FCSTD DOCUMENT  (FreeCAD 1.0R39319 (Git))
Label: Assy_PiTrac
License: All rights reserved
LicenseURL: https://en.wikipedia.org/wiki/All_rights_reserved
objects: TechDraw::DrawViewBalloon×30, App::Link×9, TechDraw::DrawProjGroupItem×6, TechDraw::DrawViewDimension×6, App::DocumentObjectGroup×3, TechDraw::DrawSVGTemplate×2, TechDraw::DrawViewSection×2, TechDraw::DrawViewAnnotation×2, TechDraw::DrawPage×2, PartDesign::CoordinateSystem×1, App::FeaturePython×1, App::Part×1, Spreadsheet::Sheet×1, TechDraw::DrawProjGroup×1, TechDraw::DrawViewSpreadsheet×1, TechDraw::DrawViewDimExtent×1
note: 15 computed .brp shape members not serialized (recipe doc carries the construction recipe); baked Part::Feature solids carry a one-line shape summary decoded from their .brp
EXTERNAL_REF file=Assy_Stack_Module_PSU.FCStd obj=LCS_Origin
EXTERNAL_REF file=Assy_Stack_Module_PSU.FCStd obj=Assembly
EXTERNAL_REF file=Assy_Stack_Module_Flight_Cam.FCStd obj=LCS_Origin
EXTERNAL_REF file=Assy_Stack_Module_Flight_Cam.FCStd obj=Assembly
EXTERNAL_REF file=Assy_Stack_Module_LED.FCStd obj=LCS_Origin
EXTERNAL_REF file=Assy_Stack_Module_LED.FCStd obj=Assembly
EXTERNAL_REF file=Assy_Stack_Module_Tee_Cam.FCStd obj=LCS_Origin
EXTERNAL_REF file=Assy_Stack_Module_Tee_Cam.FCStd obj=Assembly
EXTERNAL_REF file=Assy_Stack_Module_Cover_forInserts.FCStd obj=LCS_Origin
EXTERNAL_REF file=Assy_Stack_Module_Cover_forInserts.FCStd obj=Assembly
EXTERNAL_REF file=Assy_RaspberryPi5_carrier.FCStd obj=LCS_Origin
EXTERNAL_REF file=Assy_RaspberryPi5_carrier.FCStd obj=Assembly
EXTERNAL_REF file=Assy_V3Connector_Board.FCStd obj=LCS_Origin
EXTERNAL_REF file=Assy_V3Connector_Board.FCStd obj=Assembly
EXTERNAL_REF file=../../Part/Purchase/Acrylic_Backplate.FCStd obj=LCS_1
EXTERNAL_REF file=../../Part/Purchase/Acrylic_Backplate.FCStd obj=Part
EXTERNAL_REF file=../../Part/Purchase/Shank_Shield.FCStd obj=LCS_1
EXTERNAL_REF file=../../Part/Purchase/Shank_Shield.FCStd obj=Part

FEATURE [App::DocumentObjectGroup] Parts
FEATURE [PartDesign::CoordinateSystem] LCS_Origin
  AttacherType = Attacher::AttachEngine3D
  AttachmentSupport = -> [X_Axis]
  MapMode = 2
FEATURE [App::DocumentObjectGroup] Constraints
FEATURE [App::FeaturePython] Variables  # WARN: FeaturePython — macro-defined, semantics opaque (R4)
  Type = App::PropertyContainer
FEATURE [App::DocumentObjectGroup] Configurations
FEATURE [App::Link] Assy_Stack_Module_PSU
  AttachedBy = #LCS_Origin
  AttachedTo = Parent Assembly#LCS_Origin
  LinkedObject = -> <external Assy_Stack_Module_PSU.FCStd>#Assembly
  SolverId = Asm4EE
  expr: Placement = LCS_Origin.Placement * AttachmentOffset * Assy_Stack_Module_PSU#LCS_Origin.Placement ^ -1
FEATURE [App::Link] Assy_Stack_Module_Flight_Cam
  AttachedBy = #LCS_Origin
  AttachedTo = Assy_Stack_Module_PSU#LCS_Origin
  AttachmentOffset = pos=(116.5,43.25,33.5) rot=(-0.57735,0.57735,-0.57735;4.18879rad)
  LinkPlacement = pos=(116.5,43.25,33.5) rot=(-0.57735,0.57735,-0.57735;4.18879rad)
  LinkedObject = -> <external Assy_Stack_Module_Flight_Cam.FCStd>#Assembly
  Placement = pos=(116.5,43.25,33.5) rot=(-0.57735,0.57735,-0.57735;4.18879rad)
  SolverId = Asm4EE
  expr: Placement = Assy_Stack_Module_PSU.Placement * Assy_Stack_Module_PSU#LCS_Origin.Placement * AttachmentOffset * Assy_Stack_Module_Flight_Cam#LCS_Origin.Placement ^ -1
FEATURE [App::Link] Assy_Stack_Module_LED
  AttachedBy = #LCS_Origin
  AttachedTo = Assy_Stack_Module_Flight_Cam#LCS_Origin
  AttachmentOffset = pos=(0,0,-87.5) rot=(0,0,1;0rad)
  LinkPlacement = pos=(116.5,130.75,33.5) rot=(-0.57735,0.57735,-0.57735;4.18879rad)
  LinkedObject = -> <external Assy_Stack_Module_LED.FCStd>#Assembly
  Placement = pos=(116.5,130.75,33.5) rot=(-0.57735,0.57735,-0.57735;4.18879rad)
  SolverId = Asm4EE
  expr: Placement = Assy_Stack_Module_Flight_Cam.Placement * Assy_Stack_Module_Flight_Cam#LCS_Origin.Placement * AttachmentOffset * Assy_Stack_Module_LED#LCS_Origin.Placement ^ -1
FEATURE [App::Link] Assy_Stack_Module_Tee_Cam
  AttachedBy = #LCS_Origin
  AttachedTo = Assy_Stack_Module_LED#LCS_Origin
  AttachmentOffset = pos=(0,0,-87.5) rot=(0,0,1;0rad)
  LinkPlacement = pos=(116.5,218.25,33.5) rot=(-0.57735,0.57735,-0.57735;4.18879rad)
  LinkedObject = -> <external Assy_Stack_Module_Tee_Cam.FCStd>#Assembly
  Placement = pos=(116.5,218.25,33.5) rot=(-0.57735,0.57735,-0.57735;4.18879rad)
  SolverId = Asm4EE
  expr: Placement = Assy_Stack_Module_LED.Placement * Assy_Stack_Module_LED#LCS_Origin.Placement * AttachmentOffset * Assy_Stack_Module_Tee_Cam#LCS_Origin.Placement ^ -1
FEATURE [App::Link] Assy_Stack_Module_Cover_forInserts
  AttachedBy = #LCS_Origin
  AttachedTo = Assy_Stack_Module_Tee_Cam#LCS_Origin
  AttachmentOffset = pos=(82.5,-13.5,-84.5) rot=(0.57735,-0.57735,0.57735;2.0944rad)
  LinkPlacement = pos=(130,302.75,116) rot=(-0.57735,0.57735,-0.57735;2.0944rad)
  LinkedObject = -> <external Assy_Stack_Module_Cover_forInserts.FCStd>#Assembly
  Placement = pos=(130,302.75,116) rot=(-0.57735,0.57735,-0.57735;2.0944rad)
  SolverId = Asm4EE
  expr: Placement = Assy_Stack_Module_Tee_Cam.Placement * Assy_Stack_Module_Tee_Cam#LCS_Origin.Placement * AttachmentOffset * Assy_Stack_Module_Cover_forInserts#LCS_Origin.Placement ^ -1
FEATURE [App::Link] Assy_RaspberryPi5_carrier
  AttachedBy = #LCS_Origin
  AttachedTo = Assy_Stack_Module_Tee_Cam#LCS_Origin
  AttachmentOffset = pos=(45,105,-38.5) rot=(0.57735,-0.57735,0.57735;4.18879rad)
  LinkPlacement = pos=(11.5,256.75,78.5) rot=(0,0,1;0rad)
  LinkedObject = -> <external Assy_RaspberryPi5_carrier.FCStd>#Assembly
  Placement = pos=(11.5,256.75,78.5) rot=(0,0,1;0rad)
  SolverId = Asm4EE
  expr: Placement = Assy_Stack_Module_Tee_Cam.Placement * Assy_Stack_Module_Tee_Cam#LCS_Origin.Placement * AttachmentOffset * Assy_RaspberryPi5_carrier#LCS_Origin.Placement ^ -1
FEATURE [App::Link] Assy_V3Connector_Board
  AttachedBy = #LCS_Origin
  AttachedTo = Assy_Stack_Module_Flight_Cam#LCS_Origin
  AttachmentOffset = pos=(52,50,-55) rot=(0.707107,-0.707107,0;3.14159rad)
  LinkPlacement = pos=(66.5,98.25,85.5) rot=(-1,0,0;1.5708rad)
  LinkedObject = -> <external Assy_V3Connector_Board.FCStd>#Assembly
  Placement = pos=(66.5,98.25,85.5) rot=(-1,0,0;1.5708rad)
  SolverId = Asm4EE
  expr: Placement = Assy_Stack_Module_Flight_Cam.Placement * Assy_Stack_Module_Flight_Cam#LCS_Origin.Placement * AttachmentOffset * Assy_V3Connector_Board#LCS_Origin.Placement ^ -1
FEATURE [App::Link] Acrylic_Backplate
  AttachedBy = #LCS_1
  AttachedTo = Parent Assembly#LCS_Origin
  AttachmentOffset = pos=(11,37,117) rot=(0,0,1;0rad)
  LinkPlacement = pos=(11,37,117) rot=(0,0,1;0rad)
  LinkedObject = -> <external ../../Part/Purchase/Acrylic_Backplate.FCStd>#Part
  Placement = pos=(11,37,117) rot=(0,0,1;0rad)
  SolverId = Asm4EE
  expr: Placement = LCS_Origin.Placement * AttachmentOffset * Acrylic_Backplate#LCS_1.Placement ^ -1
FEATURE [App::Link] Shank_Shield
  AttachedBy = #LCS_1
  AttachedTo = Parent Assembly#LCS_Origin
  AttachmentOffset = pos=(-3,40,-13) rot=(0,0,1;0rad)
  LinkPlacement = pos=(-3,40,-13) rot=(0,0,1;0rad)
  LinkedObject = -> <external ../../Part/Purchase/Shank_Shield.FCStd>#Part
  Placement = pos=(-3,40,-13) rot=(0,0,1;0rad)
  SolverId = Asm4EE
  expr: Placement = LCS_Origin.Placement * AttachmentOffset * Shank_Shield#LCS_1.Placement ^ -1
FEATURE [App::Part] Assembly  label="Assy_PiTrac"
  AssemblyType = Part::Link
  Group = -> [LCS_Origin,Constraints,Variables,Configurations,Assy_Stack_Module_PSU,Assy_Stack_Module_Flight_Cam,Assy_Stack_Module_LED,Assy_Stack_Module_Tee_Cam,Assy_Stack_Module_Cover_forInserts,Assy_RaspberryPi5_carrier,Assy_V3Connector_Board,Acrylic_Backplate,Shank_Shield]
  Origin = -> Origin
  Type = Assembly
FEATURE [Spreadsheet::Sheet] Spreadsheet  label="BOM"
  cells = A1=16; B1=1; C1='Acrylic Backplate; A2=15; B2=1; C2='Acrylic Shankshield; A3=14; B3=4; C3='M5x306 mm rod; D3==306 mm; A4=13; B4=4; C4='M5 x 12 mm sleeve nut; A5=12; B5=4; C5='ISO 7380-2 M5x10 mm screw; D5='10 mm; ISO 4762 optional; A6=11; B6=12; C6='ISO 7380-2 M5x15 mm screw; D6='10–15 mm; ISO 4762 optional; A7=10; B7=4; C7='ISO 10511 M5 lock nut; A8=9; B8=4; C8='ISO 4032 M5 nut; A9=8; B9=4; C9='Foot; E9='PETG or PLA; A10=7; B10=4; C10='Carrier_Clamps; E10='PETG or PLA; A11=6; B11=1; C11='Pi 5 Assembly; A12=5; B12=1; C12='ConnectorBoardv3 Assembly; A13=4; B13=1; C13='Stack Module Cover Assembly; A14=3; B14=1; C14='PSU Stack Module Assembly; D14='-; A15=2; B15=1; C15='LED Stack Module Assembly; D15='-; A16=1; B16=2; C16='Camera Stack Module Assembly; D16='-; A17='Position; B17='Quantity; C17='Part; D17='Dimensions; E17='Material
FEATURE [TechDraw::DrawSVGTemplate] Template
  EditableTexts = approval_person=GitHub PR; creator=Stefan; date_of_issue=20.03.2026; document_type=Assembly Drawing; general_tolerances=na; identification_number=na; language_code=EN; part_material=na; revision_index=AAA; scale=1 : 1; sheet_number=1 / 1; title=Assy_PiTrac
  Height = 594
  Orientation = 1
  Template = <userpath>/Documents/PiTrac/3D Printed Parts/Enclosure Version 3/Assets/PiTrac_A1_Landscape_ISO5457_minimal.svg
  Width = 841
FEATURE [TechDraw::DrawProjGroupItem] View
  CoarseView = false
  Direction = (-0.57735,0.57735,-0.57735)
  Focus = 100
  HardHidden = false
  IsoCount = 0
  IsoHidden = false
  IsoVisible = false
  LockPosition = false
  Perspective = false
  Rotation = 0
  RotationVector = (1,0,0)
  Scale = 0.5
  ScaleType = 2
  ScrubCount = 1
  SeamHidden = false
  SeamVisible = false
  SmoothHidden = false
  SmoothVisible = true
  Source = -> [Assembly]
  Type = 0
  X = 552.509
  XDirection = (-0.707106,0,0.707106)
  Y = 140.759
FEATURE [TechDraw::DrawProjGroupItem] View001  label="Front"
  CoarseView = false
  Direction = (0,0,-1)
  Focus = 100
  HardHidden = false
  IsoCount = 0
  IsoHidden = false
  IsoVisible = false
  LockPosition = true
  Perspective = false
  Rotation = 0
  RotationVector = (1,0,0)
  Scale = 0.5
  ScaleType = 2
  ScrubCount = 1
  SeamHidden = false
  SeamVisible = false
  SmoothHidden = false
  SmoothVisible = true
  Source = -> [Assembly]
  Type = 0
  X = 0
  XDirection = (-1,0,0)
  Y = 0
FEATURE [TechDraw::DrawProjGroupItem] ProjItem  label="Left"
  CoarseView = false
  Direction = (1,0,-1e-16)
  Focus = 100
  HardHidden = false
  IsoCount = 0
  IsoHidden = false
  IsoVisible = false
  LockPosition = false
  Perspective = false
  Rotation = 0
  RotationVector = (1,0,0)
  Scale = 0.5
  ScaleType = 2
  ScrubCount = 1
  SeamHidden = false
  SeamVisible = false
  SmoothHidden = false
  SmoothVisible = true
  Source = -> [Assembly]
  Type = 1
  X = 101
  XDirection = (-1e-16,0,-1)
  Y = 0
FEATURE [TechDraw::DrawProjGroupItem] ProjItem001  label="Rear"
  CoarseView = false
  Direction = (0,0,1)
  Focus = 100
  HardHidden = false
  IsoCount = 0
  IsoHidden = false
  IsoVisible = false
  LockPosition = false
  Perspective = false
  Rotation = 0
  RotationVector = (1,0,0)
  Scale = 0.5
  ScaleType = 2
  ScrubCount = 1
  SeamHidden = false
  SeamVisible = false
  SmoothHidden = false
  SmoothVisible = true
  Source = -> [Assembly]
  Type = 3
  X = 202
  XDirection = (1,0,0)
  Y = 0
FEATURE [TechDraw::DrawProjGroupItem] ProjItem002  label="Top"
  CoarseView = false
  Direction = (0,1,0)
  Focus = 100
  HardHidden = false
  IsoCount = 0
  IsoHidden = false
  IsoVisible = false
  LockPosition = false
  Perspective = false
  Rotation = 0
  RotationVector = (1,0,0)
  Scale = 0.5
  ScaleType = 2
  ScrubCount = 1
  SeamHidden = false
  SeamVisible = false
  SmoothHidden = false
  SmoothVisible = true
  Source = -> [Assembly]
  Type = 4
  X = 0
  XDirection = (-1,0,0)
  Y = -146.779
FEATURE [TechDraw::DrawProjGroup] ProjGroup
  Anchor = -> View001
  AutoDistribute = true
  LockPosition = false
  ProjectionType = 0
  Rotation = 0
  Scale = 0.5
  ScaleType = 2
  Source = -> [Assembly]
  Views = -> [View001,ProjItem,ProjItem001,ProjItem002]
  X = 169.846
  Y = 386.4
  spacingX = 15
  spacingY = 15
FEATURE [TechDraw::DrawViewSection] SectionView  label="Section A - A"
  BaseView = -> View001
  CoarseView = false
  CutSurfaceDisplay = 2
  Direction = (1,-1e-16,0)
  FileGeomPattern = <path>\data\Mod/TechDraw/PAT/FCPAT.pat
  FileHatchPattern = <path>\data\Mod/TechDraw/Patterns/simple.svg
  Focus = 100
  FuseBeforeCut = false
  HardHidden = false
  HatchOffset = (0,0,0)
  HatchRotation = 0
  HatchScale = 1
  IsoCount = 0
  IsoHidden = false
  IsoVisible = false
  LockPosition = false
  NameGeomPattern = Diamond
  Perspective = false
  Rotation = -90
  Scale = 0.5
  ScaleType = 2
  ScrubCount = 1
  SeamHidden = false
  SeamVisible = false
  SectionDirection = 4
  SectionLineStretch = 1
  SectionNormal = (1,-1e-16,0)
  SectionOrigin = (66.5,164.89,48.5)
  SectionSymbol = A
  SmoothHidden = false
  SmoothVisible = true
  Source = -> [Assembly]
  TrimAfterCut = false
  UsePreviousCut = false
  X = 505.075
  XDirection = (-1e-16,-1,0)
  Y = 347.597
FEATURE [TechDraw::DrawViewSection] SectionView001  label="Section B - B"
  BaseView = -> View001
  CoarseView = false
  CutSurfaceDisplay = 2
  Direction = (1,-1e-16,0)
  FileGeomPattern = <path>\data\Mod/TechDraw/PAT/FCPAT.pat
  FileHatchPattern = <path>\data\Mod/TechDraw/Patterns/simple.svg
  Focus = 100
  FuseBeforeCut = false
  HardHidden = false
  HatchOffset = (0,0,0)
  HatchRotation = 0
  HatchScale = 1
  IsoCount = 0
  IsoHidden = false
  IsoVisible = false
  LockPosition = false
  NameGeomPattern = Diamond
  Perspective = false
  Rotation = -90
  Scale = 0.5
  ScaleType = 2
  ScrubCount = 1
  SeamHidden = false
  SeamVisible = false
  SectionDirection = 4
  SectionLineStretch = 1
  SectionNormal = (1,-1e-16,0)
  SectionOrigin = (0,164.89,48.5)
  SectionSymbol = B
  SmoothHidden = false
  SmoothVisible = true
  Source = -> [Assembly]
  TrimAfterCut = false
  UsePreviousCut = false
  X = 634.219
  XDirection = (-1e-16,-1,0)
  Y = 350.177
FEATURE [TechDraw::DrawViewSpreadsheet] Sheet
  CellEnd = E17
  CellStart = A1
  Font = osifont
  LineWidth = 0.35
  LockPosition = false
  Rotation = 0
  ScaleType = 2
  Source = -> Spreadsheet
  Symbol = <blob: 18577 chars omitted>
  TextSize = 12
  X = 730.475
  Y = 140.759
FEATURE [TechDraw::DrawViewBalloon] Balloon
  BubbleShape = 0
  EndType = 0
  EndTypeScale = 1
  KinkLength = 5
  LockPosition = false
  OriginX = -53.9464
  OriginY = -116.086
  Rotation = 0
  ScaleType = 0
  ShapeScale = 1
  SourceView = -> View001
  Text = 1
  TextWrapLen = -1
  X = -105
  Y = -87.7835
FEATURE [TechDraw::DrawViewBalloon] Balloon001
  BubbleShape = 0
  EndType = 0
  EndTypeScale = 1
  KinkLength = 5
  LockPosition = false
  OriginX = -57.2885
  OriginY = 56.0294
  Rotation = 0
  ScaleType = 0
  ShapeScale = 1
  SourceView = -> View001
  Text = 1
  TextWrapLen = -1
  X = -105
  Y = 91.0163
FEATURE [TechDraw::DrawViewBalloon] Balloon002
  BubbleShape = 0
  EndType = 0
  EndTypeScale = 1
  KinkLength = 5
  LockPosition = false
  OriginX = -55.6174
  OriginY = -29.193
  Rotation = 0
  ScaleType = 0
  ShapeScale = 1
  SourceView = -> View001
  Text = 2
  TextWrapLen = -1
  X = -105
  Y = 10.807
FEATURE [TechDraw::DrawViewBalloon] Balloon003
  BubbleShape = 0
  EndType = 0
  EndTypeScale = 1
  KinkLength = 5
  LockPosition = false
  OriginX = -67.3146
  OriginY = -156.191
  Rotation = 0
  ScaleType = 0
  ShapeScale = 1
  SourceView = -> View001
  Text = 3
  TextWrapLen = -1
  X = -105
  Y = -116.191
FEATURE [TechDraw::DrawViewBalloon] Balloon004
  BubbleShape = 0
  EndType = 0
  EndTypeScale = 1
  KinkLength = 5
  LockPosition = false
  OriginX = -58.9595
  OriginY = 142.923
  Rotation = 0
  ScaleType = 0
  ShapeScale = 1
  SourceView = -> View001
  Text = 4
  TextWrapLen = -1
  X = -105
  Y = 150.136
FEATURE [TechDraw::DrawViewBalloon] Balloon005
  BubbleShape = 0
  EndType = 0
  EndTypeScale = 1
  KinkLength = 5
  LockPosition = false
  OriginX = 21.6383
  OriginY = -60.9425
  Rotation = 0
  ScaleType = 0
  ShapeScale = 1
  SourceView = -> ProjItem001
  Text = 5
  TextWrapLen = -1
  X = 105
  Y = -82.7705
FEATURE [TechDraw::DrawViewBalloon] Balloon006
  BubbleShape = 0
  EndType = 0
  EndTypeScale = 1
  KinkLength = 5
  LockPosition = false
  OriginX = 19.9672
  OriginY = 84.4368
  Rotation = 0
  ScaleType = 0
  ShapeScale = 1
  SourceView = -> ProjItem001
  Text = 6
  TextWrapLen = -1
  X = 105
  Y = 92.6873
FEATURE [TechDraw::DrawViewBalloon] Balloon007
  BubbleShape = 0
  EndType = 0
  EndTypeScale = 1
  KinkLength = 5
  LockPosition = false
  OriginX = 63.5
  OriginY = -169.885
  Rotation = 0
  ScaleType = 0
  ShapeScale = 1
  SourceView = -> ProjItem001
  Text = 8
  TextWrapLen = -1
  X = 60.7895
  Y = -220
FEATURE [TechDraw::DrawViewBalloon] Balloon008
  BubbleShape = 0
  EndType = 0
  EndTypeScale = 1
  KinkLength = 5
  LockPosition = false
  OriginX = -63.5
  OriginY = -169.885
  Rotation = 0
  ScaleType = 0
  ShapeScale = 1
  SourceView = -> ProjItem001
  Text = 8
  TextWrapLen = -1
  X = -23.5
  Y = -220
FEATURE [TechDraw::DrawViewBalloon] Balloon009
  BubbleShape = 0
  EndType = 0
  EndTypeScale = 1
  KinkLength = 5
  LockPosition = false
  OriginX = 153.721
  OriginY = 42.0732
  Rotation = 0
  ScaleType = 0
  ShapeScale = 1
  SourceView = -> SectionView001
  Text = 9
  TextWrapLen = -1
  X = 175
  Y = -110
FEATURE [TechDraw::DrawViewAnnotation] Annotation001
  Font = osifont
  LineSpace = 100
  LockPosition = false
  MaxWidth = -1
  Rotation = 0
  ScaleType = 0
  Text = glue into feet
  TextSize = 5
  TextStyle = 0
  X = 752.988
  Y = 294.799
FEATURE [TechDraw::DrawViewBalloon] Balloon010
  BubbleShape = 0
  EndType = 0
  EndTypeScale = 1
  KinkLength = 5
  LockPosition = false
  OriginX = 146.418
  OriginY = 42.9281
  Rotation = 0
  ScaleType = 0
  ShapeScale = 1
  SourceView = -> SectionView001
  Text = 10
  TextWrapLen = -1
  X = 175
  Y = -77.2267
FEATURE [TechDraw::DrawViewBalloon] Balloon011
  BubbleShape = 0
  EndType = 0
  EndTypeScale = 1
  KinkLength = 5
  LockPosition = false
  OriginX = -58.0981
  OriginY = 47.677
  Rotation = 0
  ScaleType = 0
  ShapeScale = 1
  SourceView = -> SectionView
  Text = 11
  TextWrapLen = -1
  X = 110
  Y = 79.3081
FEATURE [TechDraw::DrawViewBalloon] Balloon012
  BubbleShape = 0
  EndType = 0
  EndTypeScale = 1
  KinkLength = 5
  LockPosition = false
  OriginX = 24.4992
  OriginY = -14.3372
  Rotation = 0
  ScaleType = 0
  ShapeScale = 1
  SourceView = -> Balloon011
  Text = 11
  TextWrapLen = -1
  X = 55
  Y = 0.377126
FEATURE [TechDraw::DrawViewBalloon] Balloon013
  BubbleShape = 0
  EndType = 0
  EndTypeScale = 1
  KinkLength = 5
  LockPosition = false
  OriginX = -58.5385
  OriginY = -24.6701
  Rotation = 0
  ScaleType = 0
  ShapeScale = 1
  SourceView = -> SectionView
  Text = 11
  TextWrapLen = -1
  X = -110
  Y = 77.5462
FEATURE [TechDraw::DrawViewBalloon] Balloon014
  BubbleShape = 0
  EndType = 0
  EndTypeScale = 1
  KinkLength = 5
  LockPosition = false
  OriginX = -11.7845
  OriginY = -14.2271
  Rotation = 0
  ScaleType = 0
  ShapeScale = 1
  SourceView = -> Balloon013
  Text = 11
  TextWrapLen = -1
  X = -55
  Y = -1.38475
FEATURE [TechDraw::DrawViewBalloon] Balloon015
  BubbleShape = 0
  EndType = 0
  EndTypeScale = 1
  KinkLength = 5
  LockPosition = false
  OriginX = 115.998
  OriginY = 49.6591
  Rotation = 0
  ScaleType = 0
  ShapeScale = 1
  SourceView = -> SectionView
  Text = 12
  TextWrapLen = -1
  X = 110
  Y = -99.1311
FEATURE [TechDraw::DrawViewBalloon] Balloon016
  BubbleShape = 0
  EndType = 0
  EndTypeScale = 1
  KinkLength = 5
  LockPosition = false
  OriginX = 115.998
  OriginY = -23.0184
  Rotation = 0
  ScaleType = 0
  ShapeScale = 1
  SourceView = -> SectionView
  Text = 12
  TextWrapLen = -1
  X = -110
  Y = -96.4394
FEATURE [TechDraw::DrawViewDimension] Dimension
  AngleOverride = false
  Arbitrary = false
  ArbitraryTolerances = false
  BoxCorners = (2) [(-47.5,-84.9426,-1e-07),(47.5,84.9426,1e-07)]
  EqualTolerance = true
  ExtensionAngle = 0
  FormatSpec = %.2w
  FormatSpecOverTolerance = %+.2w
  FormatSpecUnderTolerance = %+.2w
  Inverted = false
  LineAngle = 0
  LockPosition = false
  MeasureType = 1
  OverTolerance = 0
  References2D = -> [SectionView]
  Rotation = 0
  ScaleType = 0
  TheoreticalExact = false
  Type = 0
  UnderTolerance = 0
  X = 69.7674
  Y = 0.858084
FEATURE [TechDraw::DrawViewDimension] Dimension001
  AngleOverride = false
  Arbitrary = false
  ArbitraryTolerances = false
  BoxCorners = (2) [(-47.5,-84.9426,-1e-07),(47.5,84.9426,1e-07)]
  EqualTolerance = true
  ExtensionAngle = 0
  FormatSpec = %.1w
  FormatSpecOverTolerance = %+.2w
  FormatSpecUnderTolerance = %+.2w
  Inverted = false
  LineAngle = 0
  LockPosition = false
  MeasureType = 1
  OverTolerance = 0
  References2D = -> [SectionView]
  Rotation = 0
  ScaleType = 0
  TheoreticalExact = false
  Type = 0
  UnderTolerance = 0
  X = 61.0108
  Y = 93.6752
FEATURE [TechDraw::DrawViewDimension] Dimension002
  AngleOverride = false
  Arbitrary = false
  ArbitraryTolerances = false
  BoxCorners = (2) [(-47.5,-84.9426,-1e-07),(47.5,84.9426,1e-07)]
  EqualTolerance = true
  ExtensionAngle = 0
  FormatSpec = %.2w
  FormatSpecOverTolerance = %+.2w
  FormatSpecUnderTolerance = %+.2w
  Inverted = false
  LineAngle = 0
  LockPosition = false
  MeasureType = 1
  OverTolerance = 0
  References2D = -> [SectionView]
  Rotation = 0
  ScaleType = 0
  TheoreticalExact = false
  Type = 0
  UnderTolerance = 0
  X = 74.7368
  Y = -60.3801
FEATURE [TechDraw::DrawViewBalloon] Balloon017
  BubbleShape = 0
  EndType = 0
  EndTypeScale = 1
  KinkLength = 5
  LockPosition = false
  OriginX = -67.739
  OriginY = -51.0045
  Rotation = 0
  ScaleType = 0
  ShapeScale = 1
  SourceView = -> ProjItem002
  Text = 13
  TextWrapLen = -1
  X = -105
  Y = -46.4766
FEATURE [TechDraw::DrawViewBalloon] Balloon018
  BubbleShape = 0
  EndType = 0
  EndTypeScale = 1
  KinkLength = 5
  LockPosition = false
  OriginX = -65.2497
  OriginY = 64.7467
  Rotation = 0
  ScaleType = 0
  ShapeScale = 1
  SourceView = -> ProjItem002
  Text = 13
  TextWrapLen = -1
  X = -105
  Y = 76.7424
FEATURE [TechDraw::DrawViewBalloon] Balloon019
  BubbleShape = 0
  EndType = 0
  EndTypeScale = 1
  KinkLength = 5
  LockPosition = false
  OriginX = 68.5487
  OriginY = -49.7599
  Rotation = 0
  ScaleType = 0
  ShapeScale = 1
  SourceView = -> ProjItem002
  Text = 13
  TextWrapLen = -1
  X = 105
  Y = -73.8586
FEATURE [TechDraw::DrawViewBalloon] Balloon020
  BubbleShape = 0
  EndType = 0
  EndTypeScale = 1
  KinkLength = 5
  LockPosition = false
  OriginX = 65.4371
  OriginY = 64.7467
  Rotation = 0
  ScaleType = 0
  ShapeScale = 1
  SourceView = -> ProjItem002
  Text = 13
  TextWrapLen = -1
  X = 105
  Y = 40.6479
FEATURE [TechDraw::DrawViewBalloon] Balloon021
  BubbleShape = 0
  EndType = 0
  EndTypeScale = 1
  KinkLength = 5
  LockPosition = false
  OriginX = -50.9364
  OriginY = -44.159
  Rotation = 0
  ScaleType = 0
  ShapeScale = 1
  SourceView = -> ProjItem002
  Text = 11
  TextWrapLen = -1
  X = -105
  Y = -7.27059
FEATURE [TechDraw::DrawViewBalloon] Balloon022
  BubbleShape = 0
  EndType = 0
  EndTypeScale = 1
  KinkLength = 5
  LockPosition = false
  OriginX = -50.3141
  OriginY = 23.6737
  Rotation = 0
  ScaleType = 0
  ShapeScale = 1
  SourceView = -> ProjItem002
  Text = 11
  TextWrapLen = -1
  X = -105
  Y = 43.1372
FEATURE [TechDraw::DrawViewBalloon] Balloon023
  BubbleShape = 0
  EndType = 0
  EndTypeScale = 1
  KinkLength = 5
  LockPosition = false
  OriginX = 52.9908
  OriginY = -44.159
  Rotation = 0
  ScaleType = 0
  ShapeScale = 1
  SourceView = -> ProjItem002
  Text = 11
  TextWrapLen = -1
  X = 105
  Y = -20.3393
FEATURE [TechDraw::DrawViewBalloon] Balloon024
  BubbleShape = 0
  EndType = 0
  EndTypeScale = 1
  KinkLength = 5
  LockPosition = false
  OriginX = 54.8577
  OriginY = 23.0514
  Rotation = 0
  ScaleType = 0
  ShapeScale = 1
  SourceView = -> ProjItem002
  Text = 11
  TextWrapLen = -1
  X = 105
  Y = 10.7766
FEATURE [TechDraw::DrawViewDimension] Dimension003
  AngleOverride = false
  Arbitrary = false
  ArbitraryTolerances = false
  BoxCorners = (2) [(-38.5,-47.5,-1e-07),(38.5,47.5,1e-07)]
  EqualTolerance = true
  ExtensionAngle = 0
  FormatSpec = %.2w
  FormatSpecOverTolerance = %+.2w
  FormatSpecUnderTolerance = %+.2w
  Inverted = false
  LineAngle = 0
  LockPosition = false
  MeasureType = 1
  OverTolerance = 0
  References2D = -> [ProjItem002]
  Rotation = 0
  ScaleType = 0
  TheoreticalExact = false
  Type = 0
  UnderTolerance = 0
  X = 0
  Y = -81.0134
FEATURE [TechDraw::DrawViewDimension] Dimension004
  AngleOverride = false
  Arbitrary = false
  ArbitraryTolerances = false
  BoxCorners = (2) [(-38.5,-47.5,-1e-07),(38.5,47.5,1e-07)]
  EqualTolerance = true
  ExtensionAngle = 0
  FormatSpec = %.2w
  FormatSpecOverTolerance = %+.2w
  FormatSpecUnderTolerance = %+.2w
  Inverted = false
  LineAngle = 0
  LockPosition = false
  MeasureType = 1
  OverTolerance = 0
  References2D = -> [ProjItem002]
  Rotation = 0
  ScaleType = 0
  TheoreticalExact = false
  Type = 0
  UnderTolerance = 0
  X = -71.7831
  Y = -4.16176
FEATURE [TechDraw::DrawViewBalloon] Balloon025
  BubbleShape = 0
  EndType = 0
  EndTypeScale = 1
  KinkLength = 5
  LockPosition = false
  OriginX = 84.8806
  OriginY = 37.8072
  Rotation = 0
  ScaleType = 0
  ShapeScale = 1
  SourceView = -> SectionView001
  Text = 14
  TextWrapLen = -1
  X = 175
  Y = -27.9869
FEATURE [TechDraw::DrawViewBalloon] Balloon026
  BubbleShape = 0
  EndType = 0
  EndTypeScale = 1
  KinkLength = 5
  LockPosition = false
  OriginX = -117.553
  OriginY = 58.3706
  Rotation = 0
  ScaleType = 0
  ShapeScale = 1
  SourceView = -> SectionView
  Text = 15
  TextWrapLen = -1
  X = 110
  Y = 135.087
FEATURE [TechDraw::DrawViewBalloon] Balloon027
  BubbleShape = 0
  EndType = 0
  EndTypeScale = 1
  KinkLength = 5
  LockPosition = false
  OriginX = -120.043
  OriginY = -72.3162
  Rotation = 0
  ScaleType = 0
  ShapeScale = 1
  SourceView = -> SectionView
  Text = 16
  TextWrapLen = -1
  X = -110
  Y = 120.774
FEATURE [TechDraw::DrawViewBalloon] Balloon028
  BubbleShape = 0
  EndType = 0
  EndTypeScale = 1
  KinkLength = 5
  LockPosition = false
  OriginX = -111.459
  OriginY = -9.05598
  Rotation = 0
  ScaleType = 0
  ShapeScale = 1
  SourceView = -> Balloon027
  Text = 7
  TextWrapLen = -1
  X = -80.2568
  Y = -20.7942
FEATURE [TechDraw::DrawViewBalloon] Balloon029
  BubbleShape = 0
  EndType = 0
  EndTypeScale = 1
  KinkLength = 5
  LockPosition = false
  OriginX = 8.69063
  OriginY = -35.9752
  Rotation = 0
  ScaleType = 0
  ShapeScale = 1
  SourceView = -> ProjItem001
  Text = 7
  TextWrapLen = -1
  X = 105
  Y = -25.2241
FEATURE [TechDraw::DrawViewDimExtent] DimExtent
  AngleOverride = false
  Arbitrary = false
  ArbitraryTolerances = false
  BoxCorners = (2) [(-38.5,-84.9426,-1e-07),(38.5,84.9426,1e-07)]
  DirExtent = 1
  EqualTolerance = true
  ExtensionAngle = 0
  FormatSpec = %.2w
  FormatSpecOverTolerance = %+.2w
  FormatSpecUnderTolerance = %+.2w
  Inverted = false
  LineAngle = 0
  LockPosition = false
  MeasureType = 1
  OverTolerance = 0
  References2D = -> [View001]
  Rotation = 0
  ScaleType = 0
  Source = -> [View001]
  TheoreticalExact = false
  Type = 2
  UnderTolerance = 0
  X = -95.2624
  Y = -0.005061
FEATURE [TechDraw::DrawViewAnnotation] Annotation
  Font = osifont
  LineSpace = 100
  LockPosition = false
  MaxWidth = -1
  Rotation = 0
  ScaleType = 0
  Text = Not all parts are shown
  TextSize = 5
  TextStyle = 0
  X = 417.461
  Y = 140.759
FEATURE [TechDraw::DrawViewDimension] Dimension005
  AngleOverride = false
  Arbitrary = false
  ArbitraryTolerances = false
  BoxCorners = (2) [(-42.3435,-79.4375,-1e-07),(42.3435,79.4375,1e-07)]
  EqualTolerance = true
  ExtensionAngle = 0
  FormatSpec = %.2w
  FormatSpecOverTolerance = %+.2w
  FormatSpecUnderTolerance = %+.2w
  Inverted = false
  LineAngle = 0
  LockPosition = false
  MeasureType = 1
  OverTolerance = 0
  References2D = -> [SectionView001]
  Rotation = 0
  ScaleType = 0
  TheoreticalExact = false
  Type = 2
  UnderTolerance = 0
  X = 55.6125
  Y = -72.175
FEATURE [TechDraw::DrawPage] Page
  KeepUpdated = true
  NextBalloonIndex = 34
  ProjectionType = 0
  Template = -> Template
  Views = -> [View,ProjGroup,SectionView,SectionView001,Sheet,Balloon,Balloon001,Balloon002,Balloon003,Balloon004,Balloon005,Balloon006,Balloon007,Balloon008,Balloon009,Annotation001,Balloon010,Balloon011,Balloon012,Balloon013,Balloon014,Balloon015,Balloon016,Dimension,Dimension001,Dimension002,Balloon017,Balloon018,Balloon019,Balloon020,Balloon021,Balloon022,Balloon023,Balloon024,Dimension003,Dimension004,+8 more]
FEATURE [TechDraw::DrawSVGTemplate] Template001
  Height = 210
  Orientation = 1
  Template = C:/Program Files/FreeCAD 1.0/data/Mod/TechDraw/Templates/Default_Template_A4_Landscape.svg
  Width = 297
FEATURE [TechDraw::DrawProjGroupItem] View002
  CoarseView = false
  Direction = (-0.57735,0.57735,-0.57735)
  Focus = 100
  HardHidden = false
  IsoCount = 0
  IsoHidden = false
  IsoVisible = false
  LockPosition = false
  Perspective = false
  Rotation = 0
  RotationVector = (1,0,0)
  Scale = 0.5
  ScaleType = 2
  ScrubCount = 1
  SeamHidden = false
  SeamVisible = false
  SmoothHidden = false
  SmoothVisible = true
  Source = -> [Assembly]
  Type = 0
  X = 148.5
  XDirection = (-0.707106,0,0.707106)
  Y = 105
FEATURE [TechDraw::DrawPage] Page001
  KeepUpdated = true
  NextBalloonIndex = 1
  ProjectionType = 0
  Template = -> Template001
  Views = -> [View002]
note: 4 file-system paths scrubbed to <path> (originals preserved in the JSON sidecar)

RESOLVED EXTERNAL PARTS (link-assembly join: the EXTERNAL_REF files above that resolve inside this repo's crawl, each included once):
---- part ../../Part/Purchase/Acrylic_Backplate.FCStd = doc fcstd_e696c1a54f34 ----
FCSTD DOCUMENT  (FreeCAD 1.0R39319 (Git))
Label: Acrylic_Backplate
License: All rights reserved
LicenseURL: https://en.wikipedia.org/wiki/All_rights_reserved
objects: Sketcher::SketchObject×1, PartDesign::Pad×1, PartDesign::Body×1, PartDesign::CoordinateSystem×1, App::Part×1
note: 7 computed .brp shape members not serialized (recipe doc carries the construction recipe); baked Part::Feature solids carry a one-line shape summary decoded from their .brp

FEATURE [Sketcher::SketchObject] Sketch
  ArcFitTolerance = 1e-06
  AttachmentSupport = -> [XY_Plane001]
  FullyConstrained = true
  MakeInternals = false
  MapMode = 5
  sketch-geometry (4):
    g0: LineSegment StartX=0 StartY=0 StartZ=0 EndX=110 EndY=0 EndZ=0
    g1: LineSegment StartX=110 StartY=0 StartZ=0 EndX=110 EndY=267 EndZ=0
    g2: LineSegment StartX=110 StartY=267 StartZ=0 EndX=0 EndY=267 EndZ=0
    g3: LineSegment StartX=0 StartY=267 StartZ=0 EndX=0 EndY=0 EndZ=0
  constraints (11):
    c: Coincident(g0,g1)
    c: Coincident(g1,g2)
    c: Coincident(g2,g3)
    c: Coincident(g3,g0)
    c: Horizontal(g0)
    c: Horizontal(g2)
    c: Vertical(g1)
    c: Vertical(g3)
    c: Coincident(g0,g-1)
    c: DistanceX(g2,g2) = 110
    c: DistanceY(g1,g1) = 267
FEATURE [PartDesign::Pad] Pad
  Direction = (0,0,1)
  Length = 2
  Length2 = 10
  Profile = -> Sketch
  ReferenceAxis = -> Sketch [N_Axis]
  Refine = true
  Suppressed = false
  Type = 0
FEATURE [PartDesign::Body] Body  label="Acrylic_Backplate001"
  AllowCompound = false
  Group = -> [Sketch,Pad]
  Origin = -> Origin001
  Tip = -> Pad
FEATURE [PartDesign::CoordinateSystem] LCS_1
  AttacherType = Attacher::AttachEngine3D
FEATURE [App::Part] Part  label="Acrylic_Backplate"
  Group = -> [Body,LCS_1]
  Origin = -> Origin
---- part ../../Part/Purchase/Shank_Shield.FCStd = doc fcstd_9076d96c1e66 ----
FCSTD DOCUMENT  (FreeCAD 1.0R39319 (Git))
Label: Shank_Shield
License: All rights reserved
LicenseURL: https://en.wikipedia.org/wiki/All_rights_reserved
objects: Sketcher::SketchObject×1, PartDesign::Pad×1, PartDesign::Body×1, PartDesign::CoordinateSystem×1, App::Part×1
note: 7 computed .brp shape members not serialized (recipe doc carries the construction recipe); baked Part::Feature solids carry a one-line shape summary decoded from their .brp

FEATURE [Sketcher::SketchObject] Sketch
  ArcFitTolerance = 1e-06
  AttachmentSupport = -> [XY_Plane001]
  FullyConstrained = true
  MakeInternals = false
  MapMode = 5
  sketch-geometry (4):
    g0: LineSegment StartX=0 StartY=0 StartZ=0 EndX=138 EndY=0 EndZ=0
    g1: LineSegment StartX=138 StartY=0 StartZ=0 EndX=138 EndY=264 EndZ=0
    g2: LineSegment StartX=138 StartY=264 StartZ=0 EndX=0 EndY=264 EndZ=0
    g3: LineSegment StartX=0 StartY=264 StartZ=0 EndX=0 EndY=0 EndZ=0
  constraints (11):
    c: Coincident(g0,g1)
    c: Coincident(g1,g2)
    c: Coincident(g2,g3)
    c: Coincident(g3,g0)
    c: Horizontal(g0)
    c: Horizontal(g2)
    c: Vertical(g1)
    c: Vertical(g3)
    c: Coincident(g0,g-1)
    c: DistanceX(g2,g2) = 138
    c: DistanceY(g1,g1) = 264
FEATURE [PartDesign::Pad] Pad
  Direction = (0,0,1)
  Length = 4
  Length2 = 10
  Profile = -> Sketch
  ReferenceAxis = -> Sketch [N_Axis]
  Refine = true
  Suppressed = false
  Type = 0
FEATURE [PartDesign::Body] Body  label="Shank_Shield001"
  AllowCompound = false
  Group = -> [Sketch,Pad]
  Origin = -> Origin001
  Tip = -> Pad
FEATURE [PartDesign::CoordinateSystem] LCS_1
  AttacherType = Attacher::AttachEngine3D
FEATURE [App::Part] Part  label="Shank_Shield"
  Group = -> [Body,LCS_1]
  Origin = -> Origin
---- part Assy_RaspberryPi5_carrier.FCStd = doc fcstd_039efc935032 ----
FCSTD DOCUMENT  (FreeCAD 1.0R39319 (Git))
Label: Assy_RaspberryPi5_carrier
License: All rights reserved
LicenseURL: https://en.wikipedia.org/wiki/All_rights_reserved
objects: TechDraw::DrawViewBalloon×6, Part::FeaturePython×4, TechDraw::DrawProjGroupItem×4, App::DocumentObjectGroup×3, TechDraw::DrawViewDimension×3, App::Link×2, TechDraw::DrawSVGTemplate×2, TechDraw::DrawPage×2, PartDesign::CoordinateSystem×1, App::FeaturePython×1, App::Part×1, Spreadsheet::Sheet×1, TechDraw::DrawViewSpreadsheet×1, TechDraw::DrawProjGroup×1
note: 11 computed .brp shape members not serialized (recipe doc carries the construction recipe); baked Part::Feature solids carry a one-line shape summary decoded from their .brp
EXTERNAL_REF file=../../Part/Print/Pi5_Carrier_vertical_3mm.FCStd obj=LCS_1
EXTERNAL_REF file=../../Part/Print/Pi5_Carrier_vertical_3mm.FCStd obj=Part
EXTERNAL_REF file=../../Part/Print/Pi5_Carrier_vertical_3mm.FCStd obj=pi5_att
EXTERNAL_REF file=../../Part/Purchase/RaspberryPi5.FCStd obj=LCS_1
EXTERNAL_REF file=../../Part/Purchase/RaspberryPi5.FCStd obj=RP_004882_DD___Pi_5_Mechanical_Reference_3D_model_Iss1

FEATURE [App::DocumentObjectGroup] Parts
FEATURE [PartDesign::CoordinateSystem] LCS_Origin
  AttacherType = Attacher::AttachEngine3D
  AttachmentSupport = -> [X_Axis]
  MapMode = 2
FEATURE [App::DocumentObjectGroup] Constraints
FEATURE [App::FeaturePython] Variables  # WARN: FeaturePython — macro-defined, semantics opaque (R4)
  Type = App::PropertyContainer
FEATURE [App::DocumentObjectGroup] Configurations
FEATURE [App::Link] Pi5_Carrier_vertical_3mm
  AttachedBy = #LCS_1
  AttachedTo = Parent Assembly#LCS_Origin
  LinkedObject = -> <external ../../Part/Print/Pi5_Carrier_vertical_3mm.FCStd>#Part
  SolverId = Asm4EE
  expr: Placement = LCS_Origin.Placement * AttachmentOffset * Pi5_Carrier_vertical_3mm#LCS_1.Placement ^ -1
FEATURE [App::Link] RP_004882_DD___Pi_5_Mechanical_Reference_3D_model_Iss1  label="RP-004882-DD - Pi 5 Mechanical Reference 3D model Iss1"
  AttachedBy = #LCS_1
  AttachedTo = Pi5_Carrier_vertical_3mm#pi5_att
  AttachmentOffset = pos=(0,0,0) rot=(0,0,1;3.14159rad)
  LinkPlacement = pos=(76,1,5.4) rot=(-0.57735,0.57735,0.57735;4.18879rad)
  LinkedObject = -> <external ../../Part/Purchase/RaspberryPi5.FCStd>#RP_004882_DD___Pi_5_Mechanical_Reference_3D_model_Iss1
  Placement = pos=(76,1,5.4) rot=(-0.57735,0.57735,0.57735;4.18879rad)
  SolverId = Asm4EE
  expr: Placement = Pi5_Carrier_vertical_3mm.Placement * Pi5_Carrier_vertical_3mm#pi5_att.Placement * AttachmentOffset * RaspberryPi5#LCS_1.Placement ^ -1
FEATURE [Part::FeaturePython] Screw  label="ST2.2x6.5-Screw"  # WARN: FeaturePython — macro-defined, semantics opaque (R4)
  BaseObject = -> Pi5_Carrier_vertical_3mm [Body.Fillet001.Edge193]
  Diameter = 1
  Invert = false
  LeftHanded = false
  Length = 1
  LengthCustom = 6.5
  MatchOuter = false
  Offset = 1.4
  OffsetAngle = 0
  Placement = pos=(51.5,40,6.9) rot=(0,0,1;0rad)
  Thread = false
  Type = 81
FEATURE [Part::FeaturePython] Screw001  label="ST2.2x6.5-Screw004"  # WARN: FeaturePython — macro-defined, semantics opaque (R4)
  BaseObject = -> Pi5_Carrier_vertical_3mm [Body.Fillet001.Edge195]
  Diameter = 1
  Invert = false
  LeftHanded = false
  Length = 1
  LengthCustom = 6.5
  MatchOuter = false
  Offset = 1.4
  OffsetAngle = 0
  Placement = pos=(100.5,40,6.9) rot=(0,0,1;0rad)
  Thread = false
  Type = 81
FEATURE [Part::FeaturePython] Screw002  label="ST2.2x6.5-Screw005"  # WARN: FeaturePython — macro-defined, semantics opaque (R4)
  BaseObject = -> Pi5_Carrier_vertical_3mm [Body.Fillet001.Edge169]
  Diameter = 1
  Invert = false
  LeftHanded = false
  Length = 1
  LengthCustom = 6.5
  MatchOuter = false
  Offset = 1.4
  OffsetAngle = 0
  Placement = pos=(51.5,-18,6.9) rot=(0,0,1;0rad)
  Thread = false
  Type = 81
FEATURE [Part::FeaturePython] Screw003  label="ST2.2x6.5-Screw006"  # WARN: FeaturePython — macro-defined, semantics opaque (R4)
  BaseObject = -> Pi5_Carrier_vertical_3mm [Body.Fillet001.Edge179]
  Diameter = 1
  Invert = false
  LeftHanded = false
  Length = 1
  LengthCustom = 6.5
  MatchOuter = false
  Offset = 1.4
  OffsetAngle = 0
  Placement = pos=(100.5,-18,6.9) rot=(0,0,1;0rad)
  Thread = false
  Type = 81
FEATURE [App::Part] Assembly  label="Assy_RaspberryPi5_carrier"
  AssemblyType = Part::Link
  Group = -> [LCS_Origin,Constraints,Variables,Configurations,Pi5_Carrier_vertical_3mm,RP_004882_DD___Pi_5_Mechanical_Reference_3D_model_Iss1,Screw,Screw001,Screw002,Screw003]
  Origin = -> Origin
  Type = Assembly
FEATURE [Spreadsheet::Sheet] Spreadsheet  label="BOM"
  cells = A1=3; B1=4; C1='M2x10 mm self-tapping screw; D1='8-12 mm ; A2=2; B2=1; C2='Pi5 ; D2='-; A3=1; B3=1; C3='Pi5_Carrier_vertical_3mm; D3='-; E3='PETG or PLA; A4='Position; B4='Quantity; C4='Part; D4='Dimensions; E4='Material
FEATURE [TechDraw::DrawSVGTemplate] Template
  EditableTexts = approval_person=GitHub PR; creator=Stefan; date_of_issue=20.03.2026; document_type=Assembly Drawing; general_tolerances=na; identification_number=na; language_code=EN; part_material=na; revision_index=AAA; scale=1 : 1; sheet_number=1 / 1; title=Assy_RaspberryPi5_carrier
  Height = 297
  Orientation = 0
  Template = <userpath>/Documents/PiTrac/3D Printed Parts/Enclosure Version 3/Assets/PiTrac_A4_Portrait_ISO5457_minimal.svg
  Width = 210
FEATURE [TechDraw::DrawViewSpreadsheet] Sheet
  CellEnd = E4
  CellStart = A1
  Font = osifont
  LineWidth = 0.35
  LockPosition = false
  Rotation = 0
  ScaleType = 2
  Source = -> Spreadsheet
  Symbol = <blob: 4580 chars omitted>
  TextSize = 12
  X = 117.534
  Y = 84.9956
FEATURE [TechDraw::DrawProjGroupItem] View
  CoarseView = false
  Direction = (0.57735,-0.57735,0.57735)
  Focus = 100
  HardHidden = false
  IsoCount = 0
  IsoHidden = false
  IsoVisible = false
  LockPosition = false
  Perspective = false
  Rotation = 0
  RotationVector = (1,0,0)
  Scale = 0.5
  ScaleType = 2
  ScrubCount = 1
  SeamHidden = false
  SeamVisible = false
  SmoothHidden = false
  SmoothVisible = true
  Source = -> [Assembly]
  Type = 0
  X = 160.566
  XDirection = (0.707107,0.707107,0)
  Y = 132.206
FEATURE [TechDraw::DrawProjGroupItem] View001  label="Front"
  CoarseView = false
  Direction = (0,0,1)
  Focus = 100
  HardHidden = false
  IsoCount = 0
  IsoHidden = false
  IsoVisible = false
  LockPosition = true
  Perspective = false
  Rotation = 0
  RotationVector = (1,0,0)
  ScaleType = 2
  ScrubCount = 1
  SeamHidden = false
  SeamVisible = false
  SmoothHidden = false
  SmoothVisible = true
  Source = -> [Assembly]
  Type = 0
  X = 0
  XDirection = (1,0,0)
  Y = 0
FEATURE [TechDraw::DrawProjGroupItem] ProjItem  label="Left"
  CoarseView = false
  Direction = (-1,0,1e-16)
  Focus = 100
  HardHidden = false
  IsoCount = 0
  IsoHidden = false
  IsoVisible = false
  LockPosition = false
  Perspective = false
  Rotation = 0
  RotationVector = (1,0,0)
  ScaleType = 0
  ScrubCount = 1
  SeamHidden = false
  SeamVisible = false
  SmoothHidden = false
  SmoothVisible = true
  Source = -> [Assembly]
  Type = 1
  X = 81.675
  XDirection = (1e-16,0,1)
  Y = 0
FEATURE [TechDraw::DrawProjGroup] ProjGroup
  Anchor = -> View001
  AutoDistribute = true
  LockPosition = false
  ProjectionType = 0
  Rotation = 0
  ScaleType = 0
  Source = -> [Assembly]
  Views = -> [View001,ProjItem]
  X = 86.1994
  Y = 225.791
  spacingX = 15
  spacingY = 15
FEATURE [TechDraw::DrawViewBalloon] Balloon
  BubbleShape = 0
  EndType = 0
  EndTypeScale = 1
  KinkLength = 5
  LockPosition = false
  OriginX = -31.4686
  OriginY = -41.9631
  Rotation = 0
  ScaleType = 0
  ShapeScale = 1
  SourceView = -> View001
  Text = 1
  TextWrapLen = -1
  X = -43.2208
  Y = -65
FEATURE [TechDraw::DrawViewBalloon] Balloon001
  BubbleShape = 0
  EndType = 0
  EndTypeScale = 1
  KinkLength = 5
  LockPosition = false
  OriginX = 16.1596
  OriginY = -10.6287
  Rotation = 0
  ScaleType = 0
  ShapeScale = 1
  SourceView = -> Balloon
  Text = 2
  TextWrapLen = -1
  X = 18.1946
  Y = -65
FEATURE [TechDraw::DrawViewBalloon] Balloon002
  BubbleShape = 0
  EndType = 0
  EndTypeScale = 1
  KinkLength = 5
  LockPosition = false
  OriginX = -3.47658
  OriginY = -19.4023
  Rotation = 0
  ScaleType = 0
  ShapeScale = 1
  SourceView = -> Balloon001
  Text = 3
  TextWrapLen = -1
  X = -15.2288
  Y = -65
FEATURE [TechDraw::DrawViewBalloon] Balloon003
  BubbleShape = 0
  EndType = 0
  EndTypeScale = 1
  KinkLength = 5
  LockPosition = false
  OriginX = 45.8229
  OriginY = -18.9845
  Rotation = 0
  ScaleType = 0
  ShapeScale = 1
  SourceView = -> Balloon002
  Text = 3
  TextWrapLen = -1
  X = 40.3376
  Y = -65
FEATURE [TechDraw::DrawViewBalloon] Balloon004
  BubbleShape = 0
  EndType = 0
  EndTypeScale = 1
  KinkLength = 5
  LockPosition = false
  OriginX = -3.05879
  OriginY = 38.6707
  Rotation = 0
  ScaleType = 0
  ShapeScale = 1
  SourceView = -> View001
  Text = 3
  TextWrapLen = -1
  X = -18.1533
  Y = 53
FEATURE [TechDraw::DrawViewBalloon] Balloon005
  BubbleShape = 0
  EndType = 0
  EndTypeScale = 1
  KinkLength = 5
  LockPosition = false
  OriginX = 45.4051
  OriginY = 39.9241
  Rotation = 0
  ScaleType = 0
  ShapeScale = 1
  SourceView = -> Balloon004
  Text = 3
  TextWrapLen = -1
  X = 32.3995
  Y = 53
FEATURE [TechDraw::DrawViewDimension] Dimension
  AngleOverride = false
  Arbitrary = false
  ArbitraryTolerances = false
  BoxCorners = (2) [(-55,-45,-1e-07),(55,45,1e-07)]
  EqualTolerance = true
  ExtensionAngle = 0
  FormatSpec = %.2w
  FormatSpecOverTolerance = %+.2w
  FormatSpecUnderTolerance = %+.2w
  Inverted = false
  LineAngle = 0
  LockPosition = false
  MeasureType = 1
  OverTolerance = 0
  References2D = -> [View001]
  Rotation = 0
  ScaleType = 0
  TheoreticalExact = false
  Type = 0
  UnderTolerance = 0
  X = 8.83117
  Y = -68.9029
FEATURE [TechDraw::DrawViewDimension] Dimension001
  AngleOverride = false
  Arbitrary = false
  ArbitraryTolerances = false
  BoxCorners = (2) [(-55,-45,-1e-07),(55,45,1e-07)]
  EqualTolerance = true
  ExtensionAngle = 0
  FormatSpec = %.2w
  FormatSpecOverTolerance = %+.2w
  FormatSpecUnderTolerance = %+.2w
  Inverted = false
  LineAngle = 0
  LockPosition = false
  MeasureType = 1
  OverTolerance = 0
  References2D = -> [View001]
  Rotation = 0
  ScaleType = 0
  TheoreticalExact = false
  Type = 0
  UnderTolerance = 0
  X = 101.118
  Y = -0.2
FEATURE [TechDraw::DrawViewDimension] Dimension002
  AngleOverride = false
  Arbitrary = false
  ArbitraryTolerances = false
  BoxCorners = (2) [(-11.675,-45,-1e-07),(11.675,45,1e-07)]
  EqualTolerance = true
  ExtensionAngle = 0
  FormatSpec = %.2w
  FormatSpecOverTolerance = %+.2w
  FormatSpecUnderTolerance = %+.2w
  Inverted = false
  LineAngle = 0
  LockPosition = false
  MeasureType = 1
  OverTolerance = 0
  References2D = -> [ProjItem]
  Rotation = 0
  ScaleType = 0
  TheoreticalExact = false
  Type = 0
  UnderTolerance = 0
  X = -0.525
  Y = -60.4861
FEATURE [TechDraw::DrawPage] Page
  KeepUpdated = true
  NextBalloonIndex = 7
  ProjectionType = 0
  Template = -> Template
  Views = -> [Sheet,View,ProjGroup,Balloon,Balloon001,Balloon002,Balloon003,Balloon004,Balloon005,Dimension,Dimension001,Dimension002]
FEATURE [TechDraw::DrawSVGTemplate] Template001
  Height = 210
  Orientation = 1
  Template = C:/Program Files/FreeCAD 1.0/data/Mod/TechDraw/Templates/Default_Template_A4_Landscape.svg
  Width = 297
FEATURE [TechDraw::DrawProjGroupItem] View002
  CoarseView = false
  Direction = (0.57735,-0.57735,0.57735)
  Focus = 100
  HardHidden = false
  IsoCount = 0
  IsoHidden = false
  IsoVisible = false
  LockPosition = false
  Perspective = false
  Rotation = 0
  RotationVector = (1,0,0)
  Scale = 2
  ScaleType = 2
  ScrubCount = 1
  SeamHidden = false
  SeamVisible = false
  SmoothHidden = false
  SmoothVisible = true
  Source = -> [Assembly]
  Type = 0
  X = 148.5
  XDirection = (0.707107,0.707107,0)
  Y = 105
FEATURE [TechDraw::DrawPage] Page001
  KeepUpdated = true
  NextBalloonIndex = 1
  ProjectionType = 0
  Template = -> Template001
  Views = -> [View002]
---- part Assy_Stack_Module_Cover_forInserts.FCStd = doc fcstd_45fed0050b64 ----
FCSTD DOCUMENT  (FreeCAD 1.0R39319 (Git))
Label: Assy_Stack_Module_Cover_forInserts
License: All rights reserved
LicenseURL: https://en.wikipedia.org/wiki/All_rights_reserved
objects: Part::FeaturePython×13, TechDraw::DrawViewBalloon×13, App::Link×8, TechDraw::DrawProjGroupItem×7, App::DocumentObjectGroup×3, TechDraw::DrawViewDimension×3, TechDraw::DrawSVGTemplate×2, TechDraw::DrawPage×2, PartDesign::CoordinateSystem×1, App::FeaturePython×1, App::Part×1, Spreadsheet::Sheet×1, TechDraw::DrawViewSpreadsheet×1, TechDraw::DrawProjGroup×1
note: 20 computed .brp shape members not serialized (recipe doc carries the construction recipe); baked Part::Feature solids carry a one-line shape summary decoded from their .brp
EXTERNAL_REF file=../../Part/Print/Stack_Module_Cover_forInserts.FCStd obj=stack_att
EXTERNAL_REF file=../../Part/Print/Stack_Module_Cover_forInserts.FCStd obj=Part
EXTERNAL_REF file=../../Part/Purchase/M5x12_Sleeve_Nut.FCStd obj=LCS_1
EXTERNAL_REF file=../../Part/Print/Stack_Module_Cover_forInserts.FCStd obj=sleevenut_att1
EXTERNAL_REF file=../../Part/Purchase/M5x12_Sleeve_Nut.FCStd obj=Part
EXTERNAL_REF file=../../Part/Print/Stack_Module_Cover_forInserts.FCStd obj=sleevenut_att2
EXTERNAL_REF file=../../Part/Print/Stack_Module_Cover_forInserts.FCStd obj=sleevenut_att3
EXTERNAL_REF file=../../Part/Print/Stack_Module_Cover_forInserts.FCStd obj=sleevenut_att4
EXTERNAL_REF file=../../Part/Print/Stack_Module_Cover_LogoTee.FCStd obj=LCS_1
EXTERNAL_REF file=../../Part/Print/Stack_Module_Cover_forInserts.FCStd obj=tee_att
EXTERNAL_REF file=../../Part/Print/Stack_Module_Cover_LogoTee.FCStd obj=Part
EXTERNAL_REF file=../../Part/Print/Stack_Module_Cover_LogoBall.FCStd obj=LCS_1
EXTERNAL_REF file=../../Part/Print/Stack_Module_Cover_forInserts.FCStd obj=Logo_att
EXTERNAL_REF file=../../Part/Print/Stack_Module_Cover_LogoBall.FCStd obj=Part
EXTERNAL_REF file=../../Part/Print/Stack_Module_Cover_insert.FCStd obj=LCS_1
EXTERNAL_REF file=../../Part/Print/Stack_Module_Cover_insert.FCStd obj=Part

FEATURE [App::DocumentObjectGroup] Parts
FEATURE [PartDesign::CoordinateSystem] LCS_Origin
  AttacherType = Attacher::AttachEngine3D
  AttachmentSupport = -> [X_Axis]
  MapMode = 2
FEATURE [App::DocumentObjectGroup] Constraints
FEATURE [App::FeaturePython] Variables  # WARN: FeaturePython — macro-defined, semantics opaque (R4)
  Type = App::PropertyContainer
FEATURE [App::DocumentObjectGroup] Configurations
FEATURE [App::Link] Stack_Module_Cover_twoInserts
  AttachedBy = #stack_att
  AttachedTo = Parent Assembly#LCS_Origin
  AttachmentOffset = pos=(0,0,0) rot=(0.57735,0.57735,-0.57735;4.18879rad)
  LinkPlacement = pos=(-4e-16,62.5,-63.5) rot=(0.57735,0.57735,-0.57735;2.0944rad)
  LinkedObject = -> <external ../../Part/Print/Stack_Module_Cover_forInserts.FCStd>#Part
  Placement = pos=(-4e-16,62.5,-63.5) rot=(0.57735,0.57735,-0.57735;2.0944rad)
  SolverId = Asm4EE
  expr: Placement = LCS_Origin.Placement * AttachmentOffset * Stack_Module_Cover_forInserts#stack_att.Placement ^ -1
FEATURE [App::Link] M5x12_Sleeve_Nut
  AttachedBy = #LCS_1
  AttachedTo = Stack_Module_Cover_twoInserts#sleevenut_att1
  AttachmentOffset = pos=(0,0,0) rot=(0,1,0;3.14159rad)
  LinkPlacement = pos=(-8,116,-130) rot=(-0.707107,0,0.707107;3.14159rad)
  LinkedObject = -> <external ../../Part/Purchase/M5x12_Sleeve_Nut.FCStd>#Part
  Placement = pos=(-8,116,-130) rot=(-0.707107,0,0.707107;3.14159rad)
  SolverId = Asm4EE
  expr: Placement = Stack_Module_Cover_twoInserts.Placement * Stack_Module_Cover_forInserts#sleevenut_att1.Placement * AttachmentOffset * M5x12_Sleeve_Nut#LCS_1.Placement ^ -1
FEATURE [App::Link] M5x12_Sleeve_Nut001
  AttachedBy = #LCS_1
  AttachedTo = Stack_Module_Cover_twoInserts#sleevenut_att2
  AttachmentOffset = pos=(0,0,0) rot=(0,1,0;3.14159rad)
  LinkPlacement = pos=(-8,2.84e-14,-127) rot=(-0.707107,0,0.707107;3.14159rad)
  LinkedObject = -> <external ../../Part/Purchase/M5x12_Sleeve_Nut.FCStd>#Part
  Placement = pos=(-8,2.84e-14,-127) rot=(-0.707107,0,0.707107;3.14159rad)
  SolverId = Asm4EE
  expr: Placement = Stack_Module_Cover_twoInserts.Placement * Stack_Module_Cover_forInserts#sleevenut_att2.Placement * AttachmentOffset * M5x12_Sleeve_Nut#LCS_1.Placement ^ -1
FEATURE [App::Link] M5x12_Sleeve_Nut002
  AttachedBy = #LCS_1
  AttachedTo = Stack_Module_Cover_twoInserts#sleevenut_att3
  LinkPlacement = pos=(-8,1.42e-14,-1.47e-14) rot=(0,-1,0;1.5708rad)
  LinkedObject = -> <external ../../Part/Purchase/M5x12_Sleeve_Nut.FCStd>#Part
  Placement = pos=(-8,1.42e-14,-1.47e-14) rot=(0,-1,0;1.5708rad)
  SolverId = Asm4EE
  expr: Placement = Stack_Module_Cover_twoInserts.Placement * Stack_Module_Cover_forInserts#sleevenut_att3.Placement * AttachmentOffset * M5x12_Sleeve_Nut#LCS_1.Placement ^ -1
FEATURE [App::Link] M5x12_Sleeve_Nut003
  AttachedBy = #LCS_1
  AttachedTo = Stack_Module_Cover_twoInserts#sleevenut_att4
  LinkPlacement = pos=(-8,116,3) rot=(0,-1,0;1.5708rad)
  LinkedObject = -> <external ../../Part/Purchase/M5x12_Sleeve_Nut.FCStd>#Part
  Placement = pos=(-8,116,3) rot=(0,-1,0;1.5708rad)
  SolverId = Asm4EE
  expr: Placement = Stack_Module_Cover_twoInserts.Placement * Stack_Module_Cover_forInserts#sleevenut_att4.Placement * AttachmentOffset * M5x12_Sleeve_Nut#LCS_1.Placement ^ -1
FEATURE [App::Link] Stack_Module_Cover_LogoTee
  AttachedBy = #LCS_1
  AttachedTo = Stack_Module_Cover_twoInserts#tee_att
  LinkPlacement = pos=(-22.5417,59.55,-63.5) rot=(-0.706014,0.055565,0.706014;3.03058rad)
  LinkedObject = -> <external ../../Part/Print/Stack_Module_Cover_LogoTee.FCStd>#Part
  Placement = pos=(-22.5417,59.55,-63.5) rot=(-0.706014,0.055565,0.706014;3.03058rad)
  SolverId = Asm4EE
  expr: Placement = Stack_Module_Cover_twoInserts.Placement * Stack_Module_Cover_forInserts#tee_att.Placement * AttachmentOffset * Stack_Module_Cover_LogoTee#LCS_1.Placement ^ -1
FEATURE [App::Link] Stack_Module_Cover_LogoBall
  AttachedBy = #LCS_1
  AttachedTo = Stack_Module_Cover_twoInserts#Logo_att
  AttachmentOffset = pos=(0,0,0) rot=(0,1,0;3.14159rad)
  LinkPlacement = pos=(-22.7075,58.503,-63.5) rot=(-0.706014,0.055565,0.706014;3.03058rad)
  LinkedObject = -> <external ../../Part/Print/Stack_Module_Cover_LogoBall.FCStd>#Part
  Placement = pos=(-22.7075,58.503,-63.5) rot=(-0.706014,0.055565,0.706014;3.03058rad)
  SolverId = Asm4EE
  expr: Placement = Stack_Module_Cover_twoInserts.Placement * Stack_Module_Cover_forInserts#Logo_att.Placement * AttachmentOffset * Stack_Module_Cover_LogoBall#LCS_1.Placement ^ -1
FEATURE [App::Link] Stack_Module_Cover_insert
  AttachedBy = #LCS_1
  AttachedTo = Stack_Module_Cover_twoInserts#Logo_att
  LinkPlacement = pos=(-22.7075,58.503,-63.5) rot=(0.553126,-0.543555,0.631347;3.98786rad)
  LinkedObject = -> <external ../../Part/Print/Stack_Module_Cover_insert.FCStd>#Part
  Placement = pos=(-22.7075,58.503,-63.5) rot=(0.553126,-0.543555,0.631347;3.98786rad)
  SolverId = Asm4EE
  expr: Placement = Stack_Module_Cover_twoInserts.Placement * Stack_Module_Cover_forInserts#Logo_att.Placement * AttachmentOffset * Stack_Module_Cover_insert#LCS_1.Placement ^ -1
FEATURE [Part::FeaturePython] Screw  label="M5x14-Screw"  # WARN: FeaturePython — macro-defined, semantics opaque (R4)
  BaseObject = -> Stack_Module_Cover_twoInserts [Body.Pocket022.Edge443]
  Diameter = 3
  Invert = false
  LeftHanded = false
  Length = 3
  LengthCustom = 14
  MatchOuter = false
  OffsetAngle = 0
  Placement = pos=(-4.5,113.5,-13.5) rot=(0,-1,0;1.5708rad)
  Thread = false
  Type = 86
FEATURE [Part::FeaturePython] Screw001  label="M5x14-Screw007"  # WARN: FeaturePython — macro-defined, semantics opaque (R4)
  BaseObject = -> Stack_Module_Cover_twoInserts [Body.Pocket022.Edge441]
  Diameter = 3
  Invert = false
  LeftHanded = false
  Length = 3
  LengthCustom = 14
  MatchOuter = false
  OffsetAngle = 0
  Placement = pos=(-4.5,46.5,-13.5) rot=(0,-1,0;1.5708rad)
  Thread = false
  Type = 86
FEATURE [Part::FeaturePython] Screw002  label="M5x14-Screw008"  # WARN: FeaturePython — macro-defined, semantics opaque (R4)
  BaseObject = -> Stack_Module_Cover_twoInserts [Body.Pocket022.Edge440]
  Diameter = 3
  Invert = true
  LeftHanded = false
  Length = 3
  LengthCustom = 14
  MatchOuter = false
  OffsetAngle = 0
  Placement = pos=(-4.5,46.5,-113.5) rot=(0,-1,0;1.5708rad)
  Thread = false
  Type = 86
FEATURE [Part::FeaturePython] Screw003  label="M5x14-Screw009"  # WARN: FeaturePython — macro-defined, semantics opaque (R4)
  BaseObject = -> Stack_Module_Cover_twoInserts [Body.Pocket022.Edge442]
  Diameter = 3
  Invert = true
  LeftHanded = false
  Length = 3
  LengthCustom = 14
  MatchOuter = false
  OffsetAngle = 0
  Placement = pos=(-4.5,113.5,-113.5) rot=(0,-1,0;1.5708rad)
  Thread = false
  Type = 86
FEATURE [Part::FeaturePython] Screw004  label="ST2.9x9.5-Screw"  # WARN: FeaturePython — macro-defined, semantics opaque (R4)
  BaseObject = -> Stack_Module_Cover_twoInserts [Body.Pocket022.Edge623]
  Diameter = 2
  Invert = true
  LeftHanded = false
  Length = 1
  LengthCustom = 9.5
  MatchOuter = false
  OffsetAngle = 0
  Placement = pos=(-3.55191,109.13,-63.5) rot=(0.156434,0.987688,0;1.5708rad)
  Thread = false
  Type = 81
FEATURE [Part::FeaturePython] Screw005  label="ST2.9x9.5-Screw009"  # WARN: FeaturePython — macro-defined, semantics opaque (R4)
  BaseObject = -> Stack_Module_Cover_insert [Body.Pocket001.Edge17]
  Diameter = 2
  Invert = true
  LeftHanded = false
  Length = 1
  LengthCustom = 9.5
  MatchOuter = false
  OffsetAngle = 0
  Placement = pos=(-5.0963,86.5939,-63.5) rot=(0.156434,0.987688,0;1.5708rad)
  Thread = false
  Type = 81
FEATURE [Part::FeaturePython] Screw006  label="ST2.9x9.5-Screw010"  # WARN: FeaturePython — macro-defined, semantics opaque (R4)
  BaseObject = -> Stack_Module_Cover_insert [Body.Pocket001.Edge16]
  Diameter = 2
  Invert = true
  LeftHanded = false
  Length = 1
  LengthCustom = 9.5
  MatchOuter = false
  OffsetAngle = 0
  Placement = pos=(-6.92025,75.0779,-76.6923) rot=(0.156434,0.987688,0;1.5708rad)
  Thread = false
  Type = 81
FEATURE [Part::FeaturePython] Screw007  label="ST2.9x9.5-Screw011"  # WARN: FeaturePython — macro-defined, semantics opaque (R4)
  BaseObject = -> Stack_Module_Cover_insert [Body.Pocket001.Edge18]
  Diameter = 2
  Invert = true
  LeftHanded = false
  Length = 1
  LengthCustom = 9.5
  MatchOuter = false
  OffsetAngle = 0
  Placement = pos=(-6.99407,74.6118,-49.6583) rot=(0.156434,0.987688,0;1.5708rad)
  Thread = false
  Type = 81
FEATURE [Part::FeaturePython] Screw008  label="ST2.9x9.5-Screw012"  # WARN: FeaturePython — macro-defined, semantics opaque (R4)
  BaseObject = -> Stack_Module_Cover_insert [Body.Pocket001.Edge9]
  Diameter = 2
  Invert = true
  LeftHanded = false
  Length = 1
  LengthCustom = 9.5
  MatchOuter = false
  OffsetAngle = 0
  Placement = pos=(-13.4655,33.7525,-63.5) rot=(0.156434,0.987688,0;1.5708rad)
  Thread = false
  Type = 81
FEATURE [Part::FeaturePython] Screw009  label="ST2.9x6.5-Screw"  # WARN: FeaturePython — macro-defined, semantics opaque (R4)
  BaseObject = -> Stack_Module_Cover_twoInserts [Body.Pocket022.Edge118]
  Diameter = 2
  Invert = false
  LeftHanded = false
  Length = 0
  LengthCustom = 6.5
  MatchOuter = false
  Offset = 2
  OffsetAngle = 0
  Placement = pos=(-11.5578,71.3676,-103.202) rot=(0.156434,0.987688,0;1.5708rad)
  Thread = false
  Type = 81
FEATURE [Part::FeaturePython] Screw010  label="ST2.9x6.5-Screw012"  # WARN: FeaturePython — macro-defined, semantics opaque (R4)
  BaseObject = -> Stack_Module_Cover_twoInserts [Body.Pocket022.Edge121]
  Diameter = 2
  Invert = false
  LeftHanded = false
  Length = 0
  LengthCustom = 6.5
  MatchOuter = false
  Offset = 2
  OffsetAngle = 0
  Placement = pos=(-18.0667,30.2717,-95.8654) rot=(0.156434,0.987688,0;1.5708rad)
  Thread = false
  Type = 81
FEATURE [Part::FeaturePython] Screw011  label="ST2.9x6.5-Screw013"  # WARN: FeaturePython — macro-defined, semantics opaque (R4)
  BaseObject = -> Stack_Module_Cover_twoInserts [Body.Pocket022.Edge169]
  Diameter = 2
  Invert = false
  LeftHanded = false
  Length = 0
  LengthCustom = 6.5
  MatchOuter = false
  Offset = 2
  OffsetAngle = 0
  Placement = pos=(-16.0788,42.8227,-23.798) rot=(0.156434,0.987688,0;1.5708rad)
  Thread = false
  Type = 81
FEATURE [Part::FeaturePython] Screw012  label="ST2.9x6.5-Screw014"  # WARN: FeaturePython — macro-defined, semantics opaque (R4)
  BaseObject = -> Stack_Module_Cover_twoInserts [Body.Pocket022.Edge168]
  Diameter = 2
  Invert = false
  LeftHanded = false
  Length = 0
  LengthCustom = 6.5
  MatchOuter = false
  Offset = 2
  OffsetAngle = 0
  Placement = pos=(-9.5699,83.9185,-31.1346) rot=(0.156434,0.987688,0;1.5708rad)
  Thread = false
  Type = 81
FEATURE [App::Part] Assembly  label="Assy_Stack_Module_Cover_forInserts"
  AssemblyType = Part::Link
  Group = -> [LCS_Origin,Constraints,Variables,Configurations,Stack_Module_Cover_twoInserts,M5x12_Sleeve_Nut,M5x12_Sleeve_Nut001,M5x12_Sleeve_Nut002,M5x12_Sleeve_Nut003,Stack_Module_Cover_LogoTee,Stack_Module_Cover_LogoBall,Stack_Module_Cover_insert,Screw,Screw001,Screw002,Screw003,Screw004,Screw005,Screw006,Screw007,Screw008,Screw009,Screw010,Screw011,Screw012]
  Origin = -> Origin
  Type = Assembly
FEATURE [Spreadsheet::Sheet] Spreadsheet  label="BOM"
  cells = A1=6; B1=5; C1='M3x10 mm self-tapping screw; D1==10 mm; A2=5; B2=4; C2='M3x5 mm self-tapping screw; D2==5 mm; A3=4; B3=1; C3='Stack_Module_Cover_LogoBall; D3='-; E3='PETG or PLA; A4=3; B4=1; C4='Stack_Module_Cover_LogoTee; D4='-; E4='PETG or PLA; A5=2; B5=1; C5='Stack_Module_Cover_insert; D5='-; E5='PETG or PLA, white; A6=1; B6=1; C6='Stack_Module_Cover_forInserts; D6='-; E6='PETG or PLA; A7='Position; B7='Quantity; C7='Part; D7='Dimensions; E7='Material
FEATURE [TechDraw::DrawSVGTemplate] Template
  EditableTexts = approval_person=GitHubPR; creator=Stefan; date_of_issue=20.03.2026; document_type=Assembly Drawing; general_tolerances=na; identification_number=na; language_code=EN; part_material=na; revision_index=AAA; scale=1 : 1; sheet_number=1 / 1; title=Assy_Stack_Module_Cover_forInserts
  Height = 420
  Orientation = 1
  Template = <userpath>/Documents/PiTrac/3D Printed Parts/Enclosure Version 3/Assets/PiTrac_A2_Landscape_ISO5457_minimal.svg
  Width = 594
FEATURE [TechDraw::DrawViewSpreadsheet] Sheet
  CellEnd = E7
  CellStart = A1
  Font = osifont
  LineWidth = 0.35
  LockPosition = false
  Rotation = 0
  ScaleType = 2
  Source = -> Spreadsheet
  Symbol = <blob: 7887 chars omitted>
  TextSize = 12
  X = 496.686
  Y = 106.021
FEATURE [TechDraw::DrawProjGroupItem] View
  CoarseView = false
  Direction = (-0.57735,0.57735,-0.57735)
  Focus = 100
  HardHidden = false
  IsoCount = 0
  IsoHidden = false
  IsoVisible = false
  LockPosition = false
  Perspective = false
  Rotation = 0
  RotationVector = (1,0,0)
  Scale = 0.5
  ScaleType = 2
  ScrubCount = 1
  SeamHidden = false
  SeamVisible = false
  SmoothHidden = false
  SmoothVisible = true
  Source = -> [Assembly]
  Type = 0
  X = 339.537
  XDirection = (0,-0.707106,-0.707106)
  Y = 97.1596
FEATURE [TechDraw::DrawProjGroupItem] View001  label="Front"
  CoarseView = false
  Direction = (0,1,0)
  Focus = 100
  HardHidden = false
  IsoCount = 0
  IsoHidden = false
  IsoVisible = false
  LockPosition = true
  Perspective = false
  Rotation = 0
  RotationVector = (1,0,0)
  ScaleType = 2
  ScrubCount = 1
  SeamHidden = false
  SeamVisible = false
  SmoothHidden = false
  SmoothVisible = true
  Source = -> [Assembly]
  Type = 0
  X = 0
  XDirection = (0,0,-1)
  Y = 0
FEATURE [TechDraw::DrawProjGroupItem] ProjItem  label="Left"
  CoarseView = false
  Direction = (0,1e-16,1)
  Focus = 100
  HardHidden = false
  IsoCount = 0
  IsoHidden = false
  IsoVisible = false
  LockPosition = false
  Perspective = false
  Rotation = 0
  RotationVector = (1,0,0)
  ScaleType = 0
  ScrubCount = 1
  SeamHidden = false
  SeamVisible = false
  SmoothHidden = false
  SmoothVisible = true
  Source = -> [Assembly]
  Type = 1
  X = 159
  XDirection = (0,1,-1e-16)
  Y = 0
FEATURE [TechDraw::DrawProjGroupItem] ProjItem001  label="Top"
  CoarseView = false
  Direction = (-1,0,0)
  Focus = 100
  HardHidden = false
  IsoCount = 0
  IsoHidden = false
  IsoVisible = false
  LockPosition = false
  Perspective = false
  Rotation = 0
  RotationVector = (1,0,0)
  ScaleType = 0
  ScrubCount = 1
  SeamHidden = false
  SeamVisible = false
  SmoothHidden = false
  SmoothVisible = true
  Source = -> [Assembly]
  Type = 4
  X = 0
  XDirection = (0,0,-1)
  Y = -105.76
FEATURE [TechDraw::DrawProjGroupItem] ProjItem002  label="Rear"
  CoarseView = false
  Direction = (0,-1,0)
  Focus = 100
  HardHidden = false
  IsoCount = 0
  IsoHidden = false
  IsoVisible = false
  LockPosition = false
  Perspective = false
  Rotation = 0
  RotationVector = (1,0,0)
  ScaleType = 0
  ScrubCount = 1
  SeamHidden = false
  SeamVisible = false
  SmoothHidden = false
  SmoothVisible = true
  Source = -> [Assembly]
  Type = 3
  X = 318
  XDirection = (0,0,1)
  Y = 0
FEATURE [TechDraw::DrawProjGroupItem] ProjItem003  label="Bottom"
  CoarseView = false
  Direction = (1,0,0)
  Focus = 100
  HardHidden = false
  IsoCount = 0
  IsoHidden = false
  IsoVisible = false
  LockPosition = false
  Perspective = false
  Rotation = 0
  RotationVector = (1,0,0)
  ScaleType = 0
  ScrubCount = 1
  SeamHidden = false
  SeamVisible = false
  SmoothHidden = false
  SmoothVisible = true
  Source = -> [Assembly]
  Type = 5
  X = 0
  XDirection = (0,0,-1)
  Y = 105.76
FEATURE [TechDraw::DrawProjGroup] ProjGroup
  Anchor = -> View001
  AutoDistribute = true
  LockPosition = false
  ProjectionType = 0
  Rotation = 0
  ScaleType = 0
  Source = -> [Assembly]
  Views = -> [View001,ProjItem,ProjItem001,ProjItem002,ProjItem003]
  X = 165.254
  Y = 222.997
  spacingX = 15
  spacingY = 15
FEATURE [TechDraw::DrawViewBalloon] Balloon
  BubbleShape = 0
  EndType = 0
  EndTypeScale = 1
  KinkLength = 5
  LockPosition = false
  OriginX = -41.8317
  OriginY = -30.0185
  Rotation = 0
  ScaleType = 0
  ShapeScale = 1
  SourceView = -> ProjItem001
  Text = 1
  TextWrapLen = -1
  X = -90
  Y = -22.3266
FEATURE [TechDraw::DrawViewBalloon] Balloon001
  BubbleShape = 0
  EndType = 0
  EndTypeScale = 1
  KinkLength = 5
  LockPosition = false
  OriginX = -24.0534
  OriginY = 6.56381
  Rotation = 0
  ScaleType = 0
  ShapeScale = 1
  SourceView = -> ProjItem001
  Text = 2
  TextWrapLen = -1
  X = -90
  Y = -3.86449
FEATURE [TechDraw::DrawViewBalloon] Balloon002
  BubbleShape = 0
  EndType = 0
  EndTypeScale = 1
  KinkLength = 5
  LockPosition = false
  OriginX = -3.88181
  OriginY = -45.4036
  Rotation = 0
  ScaleType = 0
  ShapeScale = 1
  SourceView = -> Balloon001
  Text = 3
  TextWrapLen = -1
  X = -90
  Y = -46.6009
FEATURE [TechDraw::DrawViewBalloon] Balloon003
  BubbleShape = 0
  EndType = 0
  EndTypeScale = 1
  KinkLength = 5
  LockPosition = false
  OriginX = -29.8655
  OriginY = 27.4192
  Rotation = 0
  ScaleType = 0
  ShapeScale = 1
  SourceView = -> Balloon002
  Text = 4
  TextWrapLen = -1
  X = -90
  Y = 18.0165
FEATURE [TechDraw::DrawViewBalloon] Balloon004
  BubbleShape = 0
  EndType = 0
  EndTypeScale = 1
  KinkLength = 5
  LockPosition = false
  OriginX = -39.2761
  OriginY = -19.3115
  Rotation = 0
  ScaleType = 0
  ShapeScale = 1
  SourceView = -> ProjItem003
  Text = 5
  TextWrapLen = -1
  X = -90
  Y = -14.9656
FEATURE [TechDraw::DrawViewBalloon] Balloon005
  BubbleShape = 0
  EndType = 0
  EndTypeScale = 1
  KinkLength = 5
  LockPosition = false
  OriginX = -31.8217
  OriginY = 21.8737
  Rotation = 0
  ScaleType = 0
  ShapeScale = 1
  SourceView = -> Balloon004
  Text = 5
  TextWrapLen = -1
  X = -90
  Y = 21.0016
FEATURE [TechDraw::DrawViewBalloon] Balloon006
  BubbleShape = 0
  EndType = 0
  EndTypeScale = 1
  KinkLength = 5
  LockPosition = false
  OriginX = 33.031
  OriginY = -33.2883
  Rotation = 0
  ScaleType = 0
  ShapeScale = 1
  SourceView = -> Balloon005
  Text = 5
  TextWrapLen = -1
  X = 90
  Y = -64.3506
FEATURE [TechDraw::DrawViewBalloon] Balloon007
  BubbleShape = 0
  EndType = 0
  EndTypeScale = 1
  KinkLength = 5
  LockPosition = false
  OriginX = 40.6717
  OriginY = 7.89686
  Rotation = 0
  ScaleType = 0
  ShapeScale = 1
  SourceView = -> Balloon006
  Text = 5
  TextWrapLen = -1
  X = 90
  Y = -30.0606
FEATURE [TechDraw::DrawViewBalloon] Balloon008
  BubbleShape = 0
  EndType = 0
  EndTypeScale = 1
  KinkLength = 5
  LockPosition = false
  OriginX = 0.231897
  OriginY = 46.473
  Rotation = 0
  ScaleType = 0
  ShapeScale = 1
  SourceView = -> Balloon007
  Text = 6
  TextWrapLen = -1
  X = 90
  Y = 47.0918
FEATURE [TechDraw::DrawViewBalloon] Balloon009
  BubbleShape = 0
  EndType = 0
  EndTypeScale = 1
  KinkLength = 5
  LockPosition = false
  OriginX = -0.14082
  OriginY = 24.11
  Rotation = 0
  ScaleType = 0
  ShapeScale = 1
  SourceView = -> ProjItem003
  Text = 6
  TextWrapLen = -1
  X = 90
  Y = 32.5558
FEATURE [TechDraw::DrawViewBalloon] Balloon010
  BubbleShape = 0
  EndType = 0
  EndTypeScale = 1
  KinkLength = 5
  LockPosition = false
  OriginX = 13.8361
  OriginY = 12.5558
  Rotation = 0
  ScaleType = 0
  ShapeScale = 1
  SourceView = -> Balloon009
  Text = 6
  TextWrapLen = -1
  X = 90
  Y = 16.529
FEATURE [TechDraw::DrawViewBalloon] Balloon011
  BubbleShape = 0
  EndType = 0
  EndTypeScale = 1
  KinkLength = 5
  LockPosition = false
  OriginX = -13.1859
  OriginY = 12.9285
  Rotation = 0
  ScaleType = 0
  ShapeScale = 1
  SourceView = -> Balloon010
  Text = 6
  TextWrapLen = -1
  X = -90
  Y = 5.72021
FEATURE [TechDraw::DrawViewBalloon] Balloon012
  BubbleShape = 0
  EndType = 0
  EndTypeScale = 1
  KinkLength = 5
  LockPosition = false
  OriginX = -0.886254
  OriginY = -27.6976
  Rotation = 0
  ScaleType = 0
  ShapeScale = 1
  SourceView = -> Balloon011
  Text = 6
  TextWrapLen = -1
  X = -90
  Y = -39.5649
FEATURE [TechDraw::DrawViewDimension] Dimension
  AngleOverride = false
  Arbitrary = false
  ArbitraryTolerances = false
  BoxCorners = (2) [(-70,-16.0101,-1e-07),(70,16.0101,1e-07)]
  EqualTolerance = true
  ExtensionAngle = 0
  FormatSpec = %.2w
  FormatSpecOverTolerance = %+.2w
  FormatSpecUnderTolerance = %+.2w
  Inverted = false
  LineAngle = 0
  LockPosition = false
  MeasureType = 1
  OverTolerance = 0
  References2D = -> [ProjItem]
  Rotation = 0
  ScaleType = 0
  TheoreticalExact = false
  Type = 0
  UnderTolerance = 0
  X = 0
  Y = -52.3681
FEATURE [TechDraw::DrawViewDimension] Dimension001
  AngleOverride = false
  Arbitrary = false
  ArbitraryTolerances = false
  BoxCorners = (2) [(-74,-16.0101,-1e-07),(74,16.0101,1e-07)]
  EqualTolerance = true
  ExtensionAngle = 0
  FormatSpec = %.2w
  FormatSpecOverTolerance = %+.2w
  FormatSpecUnderTolerance = %+.2w
  Inverted = false
  LineAngle = 0
  LockPosition = false
  MeasureType = 1
  OverTolerance = 0
  References2D = -> [ProjItem002]
  Rotation = 0
  ScaleType = 0
  TheoreticalExact = false
  Type = 0
  UnderTolerance = 0
  X = 88.8831
  Y = -0.010122
FEATURE [TechDraw::DrawViewDimension] Dimension002
  AngleOverride = false
  Arbitrary = false
  ArbitraryTolerances = false
  BoxCorners = (2) [(-74,-70,-1e-07),(74,70,1e-07)]
  EqualTolerance = true
  ExtensionAngle = 0
  FormatSpec = %.2w
  FormatSpecOverTolerance = %+.2w
  FormatSpecUnderTolerance = %+.2w
  Inverted = false
  LineAngle = 0
  LockPosition = false
  MeasureType = 1
  OverTolerance = 0
  References2D = -> [ProjItem001]
  Rotation = 0
  ScaleType = 0
  TheoreticalExact = false
  Type = 0
  UnderTolerance = 0
  X = 0
  Y = -89.7283
FEATURE [TechDraw::DrawPage] Page
  KeepUpdated = true
  NextBalloonIndex = 14
  ProjectionType = 0
  Template = -> Template
  Views = -> [Sheet,View,ProjGroup,Balloon,Balloon001,Balloon002,Balloon003,Balloon004,Balloon005,Balloon006,Balloon007,Balloon008,Balloon009,Balloon010,Balloon011,Balloon012,Dimension,Dimension001,Dimension002]
FEATURE [TechDraw::DrawSVGTemplate] Template001
  Height = 210
  Orientation = 1
  Template = C:/Program Files/FreeCAD 1.0/data/Mod/TechDraw/Templates/Default_Template_A4_Landscape.svg
  Width = 297
FEATURE [TechDraw::DrawProjGroupItem] View002
  CoarseView = false
  Direction = (-0.57735,0.57735,-0.57735)
  Focus = 100
  HardHidden = false
  IsoCount = 0
  IsoHidden = false
  IsoVisible = false
  LockPosition = false
  Perspective = false
  Rotation = 0
  RotationVector = (1,0,0)
  ScaleType = 0
  ScrubCount = 1
  SeamHidden = false
  SeamVisible = false
  SmoothHidden = false
  SmoothVisible = true
  Source = -> [Assembly]
  Type = 0
  X = 148.5
  XDirection = (0,-0.707106,-0.707106)
  Y = 105
FEATURE [TechDraw::DrawPage] Page001
  KeepUpdated = true
  NextBalloonIndex = 1
  ProjectionType = 0
  Template = -> Template001
  Views = -> [View002]
---- part Assy_Stack_Module_Flight_Cam.FCStd = doc fcstd_6ac7a8e7157f ----
FCSTD DOCUMENT  (FreeCAD 1.0R39319 (Git))
Label: Assy_Stack_Module_Flight_Cam
License: All rights reserved
LicenseURL: https://en.wikipedia.org/wiki/All_rights_reserved
objects: TechDraw::DrawViewBalloon×8, TechDraw::DrawViewDimension×6, TechDraw::DrawProjGroupItem×5, App::DocumentObjectGroup×3, App::Link×3, PartDesign::CoordinateSystem×2, TechDraw::DrawSVGTemplate×2, TechDraw::DrawPage×2, App::FeaturePython×1, Spreadsheet::Sheet×1, TechDraw::DrawViewSpreadsheet×1, TechDraw::DrawViewAnnotation×1, App::Part×1, TechDraw::DrawViewSection×1, TechDraw::DrawProjGroup×1
note: 6 computed .brp shape members not serialized (recipe doc carries the construction recipe); baked Part::Feature solids carry a one-line shape summary decoded from their .brp
EXTERNAL_REF file=Assy_Stack_Module.FCStd obj=LCS_Origin
EXTERNAL_REF file=Assy_Stack_Module.FCStd obj=Assembly
EXTERNAL_REF file=Assy_Flight_Cam.FCStd obj=LCS_Origin
EXTERNAL_REF file=Assy_Flight_Cam.FCStd obj=Assembly
EXTERNAL_REF file=../../Part/Print/Variants/IRFilter_Mount_1inchround.FCStd obj=LCS_1
EXTERNAL_REF file=../../Part/Print/Variants/IRFilter_Mount_1inchround.FCStd obj=Part

FEATURE [App::DocumentObjectGroup] Parts
FEATURE [PartDesign::CoordinateSystem] LCS_Origin
  AttacherType = Attacher::AttachEngine3D
  AttachmentSupport = -> [X_Axis]
  MapMode = 2
FEATURE [App::DocumentObjectGroup] Constraints
FEATURE [App::FeaturePython] Variables  # WARN: FeaturePython — macro-defined, semantics opaque (R4)
  Type = App::PropertyContainer
FEATURE [App::DocumentObjectGroup] Configurations
FEATURE [App::Link] Assy_Stack_Module
  AttachedBy = #LCS_Origin
  AttachedTo = Parent Assembly#LCS_Origin
  LinkedObject = -> <external Assy_Stack_Module.FCStd>#Assembly
  SolverId = Asm4EE
  expr: Placement = LCS_Origin.Placement * AttachmentOffset * Assy_Stack_Module#LCS_Origin.Placement ^ -1
FEATURE [App::Link] Assy_Flight_Cam
  AttachedBy = #LCS_Origin
  AttachedTo = Assy_Stack_Module#LCS_Origin
  AttachmentOffset = pos=(0,50,-41.75) rot=(0.57735,-0.57735,0.57735;2.0944rad)
  LinkPlacement = pos=(0,50,-41.75) rot=(0.57735,-0.57735,0.57735;2.0944rad)
  LinkedObject = -> <external Assy_Flight_Cam.FCStd>#Assembly
  Placement = pos=(0,50,-41.75) rot=(0.57735,-0.57735,0.57735;2.0944rad)
  SolverId = Asm4EE
  expr: Placement = Assy_Stack_Module.Placement * Assy_Stack_Module#LCS_Origin.Placement * AttachmentOffset * Assy_Flight_Cam#LCS_Origin.Placement ^ -1
FEATURE [PartDesign::CoordinateSystem] LCS_1
  AttacherType = Attacher::AttachEngine3D
FEATURE [Spreadsheet::Sheet] Spreadsheet  label="BOM"
  cells = A1=4; B1=2; C1='ISO 7380-2 M5x10 mm screw; D1='10–15 mm; ISO 4762 optional; A2=3; B2=4; C2='Spacer; D2='-; E2='PETG or PLA; A3=2; B3=3; C3='Stack_Module; D3='-; E3='PETG or PLA; A4=1; B4=1; C4='Eyeball Assembly; D4='-; A5='Position; B5='Quantity; C5='Part; D5='Dimensions; E5='Material
FEATURE [TechDraw::DrawSVGTemplate] Template
  EditableTexts = approval_person=GitHubPR; creator=Stefan; date_of_issue=20.03.2026; document_type=Assembly Drawing; general_tolerances=na; identification_number=na; language_code=EN; part_material=na; revision_index=AAA; scale=1 : 1; sheet_number=1 / 1; title=Assy_Stack_Module_Flight_Cam
  Height = 420
  Orientation = 1
  Template = <userpath>/Documents/PiTrac/3D Printed Parts/Enclosure Version 3/Assets/PiTrac_A2_Landscape_ISO5457_minimal.svg
  Width = 594
FEATURE [TechDraw::DrawViewSpreadsheet] Sheet
  CellEnd = E5
  CellStart = A1
  Font = osifont
  LineWidth = 0.35
  LockPosition = false
  Rotation = 0
  ScaleType = 2
  Source = -> Spreadsheet
  Symbol = <blob: 5666 chars omitted>
  TextSize = 12
  X = 491.96
  Y = 97.1596
FEATURE [TechDraw::DrawViewAnnotation] Annotation
  Font = osifont
  LineSpace = 100
  LockPosition = false
  MaxWidth = -1
  Rotation = 0
  ScaleType = 0
  Text = Not all parts are shown
  TextSize = 5
  TextStyle = 0
  X = 217.611
  Y = 30.4897
FEATURE [App::Link] IRFilter_Mount_1inchround
  AttachedBy = #LCS_1
  AttachedTo = Assy_Flight_Cam#LCS_Origin
  AttachmentOffset = pos=(0,34,0) rot=(0.57735,-0.57735,0.57735;2.0944rad)
  LinkPlacement = pos=(-34,50,-41.75) rot=(0.57735,-0.57735,0.57735;4.18879rad)
  LinkedObject = -> <external ../../Part/Print/Variants/IRFilter_Mount_1inchround.FCStd>#Part
  Placement = pos=(-34,50,-41.75) rot=(0.57735,-0.57735,0.57735;4.18879rad)
  SolverId = Asm4EE
  expr: Placement = Assy_Flight_Cam.Placement * Assy_Flight_Cam#LCS_Origin.Placement * AttachmentOffset * IRFilter_Mount_1inchround#LCS_1.Placement ^ -1
FEATURE [App::Part] Assembly  label="Assy_Stack_Module_Flight_Cam"
  AssemblyType = Part::Link
  Group = -> [LCS_Origin,Constraints,Variables,Configurations,Assy_Stack_Module,Assy_Flight_Cam,LCS_1,IRFilter_Mount_1inchround]
  Origin = -> Origin
  Type = Assembly
FEATURE [TechDraw::DrawProjGroupItem] View
  CoarseView = false
  Direction = (-0.57735,0.57735,-0.577351)
  Focus = 100
  HardHidden = false
  IsoCount = 0
  IsoHidden = false
  IsoVisible = false
  LockPosition = false
  Perspective = false
  Rotation = 0
  RotationVector = (1,0,0)
  Scale = 0.5
  ScaleType = 2
  ScrubCount = 1
  SeamHidden = false
  SeamVisible = false
  SmoothHidden = false
  SmoothVisible = true
  Source = -> [Assembly]
  Type = 0
  X = 343.081
  XDirection = (0.707107,0.707107,0)
  Y = 85.3438
FEATURE [TechDraw::DrawProjGroupItem] View001  label="Front"
  CoarseView = false
  Direction = (-1,0,0)
  Focus = 100
  HardHidden = false
  IsoCount = 0
  IsoHidden = false
  IsoVisible = false
  LockPosition = true
  Perspective = false
  Rotation = 0
  RotationVector = (1,0,0)
  ScaleType = 2
  ScrubCount = 1
  SeamHidden = false
  SeamVisible = false
  SmoothHidden = false
  SmoothVisible = true
  Source = -> [Assembly]
  Type = 0
  X = 0
  XDirection = (0,1,0)
  Y = 0
FEATURE [TechDraw::DrawProjGroupItem] ProjItem001  label="Left"
  CoarseView = false
  Direction = (-1e-16,-1,0)
  Focus = 100
  HardHidden = false
  IsoCount = 0
  IsoHidden = false
  IsoVisible = false
  LockPosition = false
  Perspective = false
  Rotation = 0
  RotationVector = (1,0,0)
  ScaleType = 0
  ScrubCount = 1
  SeamHidden = false
  SeamVisible = false
  SmoothHidden = false
  SmoothVisible = true
  Source = -> [Assembly]
  Type = 1
  X = 159
  XDirection = (-1,1e-16,0)
  Y = 0
FEATURE [TechDraw::DrawViewSection] SectionView  label="Section A - A"
  BaseView = -> View001
  CoarseView = false
  CutSurfaceDisplay = 2
  Direction = (0,1,0)
  FileGeomPattern = <path>\data\Mod/TechDraw/PAT/FCPAT.pat
  FileHatchPattern = <path>\data\Mod/TechDraw/Patterns/simple.svg
  Focus = 100
  FuseBeforeCut = false
  HardHidden = false
  HatchOffset = (0,0,0)
  HatchRotation = 0
  HatchScale = 1
  IsoCount = 0
  IsoHidden = false
  IsoVisible = false
  LockPosition = false
  NameGeomPattern = Diamond
  Perspective = false
  Rotation = 90
  ScaleType = 0
  ScrubCount = 1
  SeamHidden = false
  SeamVisible = false
  SectionDirection = 4
  SectionLineStretch = 1
  SectionNormal = (0,1,0)
  SectionOrigin = (19.99,50,-39.75)
  SectionSymbol = A
  SmoothHidden = false
  SmoothVisible = true
  Source = -> [Assembly]
  TrimAfterCut = false
  UsePreviousCut = false
  X = 376.166
  XDirection = (0,0,-1)
  Y = 208.818
FEATURE [TechDraw::DrawProjGroupItem] ProjItem  label="Top"
  CoarseView = false
  Direction = (0,0,-1)
  Focus = 100
  HardHidden = false
  IsoCount = 0
  IsoHidden = false
  IsoVisible = false
  LockPosition = false
  Perspective = false
  Rotation = 0
  RotationVector = (1,0,0)
  ScaleType = 0
  ScrubCount = 1
  SeamHidden = false
  SeamVisible = false
  SmoothHidden = false
  SmoothVisible = true
  Source = -> [Assembly]
  Type = 4
  X = 0
  XDirection = (0,1,0)
  Y = -131.75
FEATURE [TechDraw::DrawProjGroup] ProjGroup
  Anchor = -> View001
  AutoDistribute = true
  LockPosition = false
  ProjectionType = 0
  Rotation = 0
  ScaleType = 0
  Source = -> [Assembly]
  Views = -> [View001,ProjItem,ProjItem001]
  X = 135.715
  Y = 324.613
  spacingX = 15
  spacingY = 15
FEATURE [TechDraw::DrawViewBalloon] Balloon
  BubbleShape = 0
  EndType = 0
  EndTypeScale = 1
  KinkLength = 5
  LockPosition = false
  OriginX = -8.10485
  OriginY = -28.1923
  Rotation = 0
  ScaleType = 0
  ShapeScale = 1
  SourceView = -> ProjItem
  Text = 1
  TextWrapLen = -1
  X = -90
  Y = -44.8211
FEATURE [TechDraw::DrawViewBalloon] Balloon001
  BubbleShape = 0
  EndType = 0
  EndTypeScale = 1
  KinkLength = 5
  LockPosition = false
  OriginX = -59
  OriginY = 4.65153
  Rotation = 0
  ScaleType = 0
  ShapeScale = 1
  SourceView = -> ProjItem
  Text = 2
  TextWrapLen = -1
  X = -90
  Y = 7.51869
FEATURE [TechDraw::DrawViewBalloon] Balloon002
  BubbleShape = 0
  EndType = 0
  EndTypeScale = 1
  KinkLength = 5
  LockPosition = false
  OriginX = -63.6389
  OriginY = -53.0053
  Rotation = 0
  ScaleType = 0
  ShapeScale = 1
  SourceView = -> ProjItem
  Text = 3
  TextWrapLen = -1
  X = -90
  Y = -71.4065
FEATURE [TechDraw::DrawViewBalloon] Balloon003
  BubbleShape = 0
  EndType = 0
  EndTypeScale = 1
  KinkLength = 5
  LockPosition = false
  OriginX = 63.25
  OriginY = -53.5
  Rotation = 0
  ScaleType = 0
  ShapeScale = 1
  SourceView = -> ProjItem
  Text = 3
  TextWrapLen = -1
  X = 90
  Y = -71.3104
FEATURE [TechDraw::DrawViewBalloon] Balloon005
  BubbleShape = 0
  EndType = 0
  EndTypeScale = 1
  KinkLength = 5
  LockPosition = false
  OriginX = 60.25
  OriginY = 62.5
  Rotation = 0
  ScaleType = 0
  ShapeScale = 1
  SourceView = -> ProjItem
  Text = 3
  TextWrapLen = -1
  X = 90
  Y = 35.237
FEATURE [TechDraw::DrawViewBalloon] Balloon006
  BubbleShape = 0
  EndType = 0
  EndTypeScale = 1
  KinkLength = 5
  LockPosition = false
  OriginX = -59.5034
  OriginY = 64.5614
  Rotation = 0
  ScaleType = 0
  ShapeScale = 1
  SourceView = -> ProjItem
  Text = 3
  TextWrapLen = -1
  X = -90
  Y = 62.1115
FEATURE [TechDraw::DrawViewBalloon] Balloon007
  BubbleShape = 0
  EndType = 0
  EndTypeScale = 1
  KinkLength = 5
  LockPosition = false
  OriginX = -51.8231
  OriginY = -46.9426
  Rotation = 0
  ScaleType = 0
  ShapeScale = 1
  SourceView = -> View001
  Text = 4
  TextWrapLen = -1
  X = -90
  Y = -51.1449
FEATURE [TechDraw::DrawViewBalloon] Balloon008
  BubbleShape = 0
  EndType = 0
  EndTypeScale = 1
  KinkLength = 5
  LockPosition = false
  OriginX = 52.1555
  OriginY = -45.761
  Rotation = 0
  ScaleType = 0
  ShapeScale = 1
  SourceView = -> View001
  Text = 4
  TextWrapLen = -1
  X = 90
  Y = -74.0359
FEATURE [TechDraw::DrawViewDimension] Dimension001
  AngleOverride = false
  Arbitrary = false
  ArbitraryTolerances = false
  BoxCorners = (2) [(-74,-70,-1e-07),(74,70,1e-07)]
  EqualTolerance = true
  ExtensionAngle = 0
  FormatSpec = %.2w
  FormatSpecOverTolerance = %+.2w
  FormatSpecUnderTolerance = %+.2w
  Inverted = false
  LineAngle = 0
  LockPosition = false
  MeasureType = 1
  OverTolerance = 0
  References2D = -> [ProjItem]
  Rotation = 0
  ScaleType = 0
  TheoreticalExact = false
  Type = 0
  UnderTolerance = 0
  X = -3.00169
  Y = -115.966
FEATURE [TechDraw::DrawViewDimension] Dimension002
  AngleOverride = false
  Arbitrary = false
  ArbitraryTolerances = false
  BoxCorners = (2) [(-70,-46,-1e-07),(70,46,1e-07)]
  EqualTolerance = true
  ExtensionAngle = 0
  FormatSpec = %.2w
  FormatSpecOverTolerance = %+.2w
  FormatSpecUnderTolerance = %+.2w
  Inverted = false
  LineAngle = 0
  LockPosition = false
  MeasureType = 1
  OverTolerance = 0
  References2D = -> [ProjItem001]
  Rotation = 0
  ScaleType = 0
  TheoreticalExact = false
  Type = 0
  UnderTolerance = 0
  X = 110.964
  Y = 0.25
FEATURE [TechDraw::DrawViewDimension] Dimension003
  AngleOverride = false
  Arbitrary = false
  ArbitraryTolerances = false
  BoxCorners = (2) [(-70,-46,-1e-07),(70,46,1e-07)]
  EqualTolerance = true
  ExtensionAngle = 0
  FormatSpec = %.2w
  FormatSpecOverTolerance = %+.2w
  FormatSpecUnderTolerance = %+.2w
  Inverted = false
  LineAngle = 0
  LockPosition = false
  MeasureType = 1
  OverTolerance = 0
  References2D = -> [ProjItem001]
  Rotation = 0
  ScaleType = 0
  TheoreticalExact = false
  Type = 0
  UnderTolerance = 0
  X = 149.356
  Y = 1.25
FEATURE [TechDraw::DrawViewDimension] Dimension004
  AngleOverride = false
  Arbitrary = false
  ArbitraryTolerances = false
  BoxCorners = (2) [(-74,-70,-1e-07),(74,70,1e-07)]
  EqualTolerance = true
  ExtensionAngle = 0
  FormatSpec = %.2w
  FormatSpecOverTolerance = %+.2w
  FormatSpecUnderTolerance = %+.2w
  Inverted = false
  LineAngle = 0
  LockPosition = false
  MeasureType = 1
  OverTolerance = 0
  References2D = -> [ProjItem]
  Rotation = 0
  ScaleType = 0
  TheoreticalExact = false
  Type = 0
  UnderTolerance = 0
  X = 126.237
  Y = 5
FEATURE [TechDraw::DrawSVGTemplate] Template001
  Height = 210
  Orientation = 1
  Template = C:/Program Files/FreeCAD 1.0/data/Mod/TechDraw/Templates/Default_Template_A4_Landscape.svg
  Width = 297
FEATURE [TechDraw::DrawProjGroupItem] View002
  CoarseView = false
  Direction = (-0.57735,0.57735,-0.577351)
  Focus = 100
  HardHidden = false
  IsoCount = 0
  IsoHidden = false
  IsoVisible = false
  LockPosition = false
  Perspective = false
  Rotation = 0
  RotationVector = (1,0,0)
  ScaleType = 0
  ScrubCount = 1
  SeamHidden = false
  SeamVisible = false
  SmoothHidden = false
  SmoothVisible = true
  Source = -> [Assembly]
  Type = 0
  X = 148.5
  XDirection = (0.707107,0.707107,0)
  Y = 105
FEATURE [TechDraw::DrawPage] Page001
  KeepUpdated = true
  NextBalloonIndex = 1
  ProjectionType = 0
  Template = -> Template001
  Views = -> [View002]
FEATURE [TechDraw::DrawViewDimension] Dimension
  AngleOverride = false
  Arbitrary = false
  ArbitraryTolerances = false
  BoxCorners = (2) [(-74,-70,-1e-07),(74,70,1e-07)]
  EqualTolerance = true
  ExtensionAngle = 0
  FormatSpec = %.1w
  FormatSpecOverTolerance = %+.2w
  FormatSpecUnderTolerance = %+.2w
  Inverted = false
  LineAngle = 0
  LockPosition = false
  MeasureType = 1
  OverTolerance = 0
  References2D = -> [ProjItem]
  Rotation = 0
  ScaleType = 0
  TheoreticalExact = false
  Type = 2
  UnderTolerance = 0
  X = 103.142
  Y = -44.9928
FEATURE [TechDraw::DrawViewDimension] Dimension005
  AngleOverride = false
  Arbitrary = false
  ArbitraryTolerances = false
  BoxCorners = (2) [(-70,-46.125,-1e-07),(70,46.125,1e-07)]
  EqualTolerance = true
  ExtensionAngle = 0
  FormatSpec = %.1w
  FormatSpecOverTolerance = %+.2w
  FormatSpecUnderTolerance = %+.2w
  Inverted = false
  LineAngle = 0
  LockPosition = false
  MeasureType = 1
  OverTolerance = 0
  References2D = -> [SectionView]
  Rotation = 0
  ScaleType = 0
  TheoreticalExact = false
  Type = 0
  UnderTolerance = 0
  X = -39.9928
  Y = -51.5552
FEATURE [TechDraw::DrawPage] Page
  KeepUpdated = true
  NextBalloonIndex = 11
  ProjectionType = 0
  Template = -> Template
  Views = -> [Sheet,View,ProjGroup,SectionView,Balloon,Balloon001,Balloon002,Balloon003,Balloon005,Balloon006,Balloon007,Balloon008,Dimension001,Dimension002,Dimension003,Dimension004,Annotation,Dimension,Dimension005]
note: 2 file-system paths scrubbed to <path> (originals preserved in the JSON sidecar)
---- part Assy_Stack_Module_LED.FCStd = doc fcstd_ca12dc1faf30 ----
FCSTD DOCUMENT  (FreeCAD 1.0R39319 (Git))
Label: Assy_Stack_Module_LED
License: All rights reserved
LicenseURL: https://en.wikipedia.org/wiki/All_rights_reserved
objects: App::DocumentObjectGroup×3, App::Link×2, PartDesign::CoordinateSystem×1, App::FeaturePython×1, App::Part×1, TechDraw::DrawSVGTemplate×1, TechDraw::DrawProjGroupItem×1, TechDraw::DrawPage×1
note: 1 computed .brp shape members not serialized (recipe doc carries the construction recipe); baked Part::Feature solids carry a one-line shape summary decoded from their .brp
EXTERNAL_REF file=Assy_Stack_Module.FCStd obj=LCS_Origin
EXTERNAL_REF file=Assy_Stack_Module.FCStd obj=Assembly
EXTERNAL_REF file=Assy_Screen_PiTracIRLED.FCStd obj=LCS_Origin
EXTERNAL_REF file=Assy_Screen_PiTracIRLED.FCStd obj=Assembly

FEATURE [App::DocumentObjectGroup] Parts
FEATURE [PartDesign::CoordinateSystem] LCS_Origin
  AttacherType = Attacher::AttachEngine3D
  AttachmentSupport = -> [X_Axis]
  MapMode = 2
FEATURE [App::DocumentObjectGroup] Constraints
FEATURE [App::FeaturePython] Variables  # WARN: FeaturePython — macro-defined, semantics opaque (R4)
  Type = App::PropertyContainer
FEATURE [App::DocumentObjectGroup] Configurations
FEATURE [App::Link] Assy_Stack_Module
  AttachedBy = #LCS_Origin
  AttachedTo = Parent Assembly#LCS_Origin
  LinkedObject = -> <external Assy_Stack_Module.FCStd>#Assembly
  SolverId = Asm4EE
  expr: Placement = LCS_Origin.Placement * AttachmentOffset * Assy_Stack_Module#LCS_Origin.Placement ^ -1
FEATURE [App::Link] Assy_Screen_PiTracIRLED
  AttachedBy = #LCS_Origin
  AttachedTo = Assy_Stack_Module#LCS_Origin
  AttachmentOffset = pos=(0,50,-41.75) rot=(0.707107,0,-0.707107;3.14159rad)
  LinkPlacement = pos=(0,50,-41.75) rot=(0.707107,0,-0.707107;3.14159rad)
  LinkedObject = -> <external Assy_Screen_PiTracIRLED.FCStd>#Assembly
  Placement = pos=(0,50,-41.75) rot=(0.707107,0,-0.707107;3.14159rad)
  SolverId = Asm4EE
  expr: Placement = Assy_Stack_Module.Placement * Assy_Stack_Module#LCS_Origin.Placement * AttachmentOffset * Assy_Screen_PiTracIRLED#LCS_Origin.Placement ^ -1
FEATURE [App::Part] Assembly  label="Assy_Stack_Module_LED"
  AssemblyType = Part::Link
  Group = -> [LCS_Origin,Constraints,Variables,Configurations,Assy_Stack_Module,Assy_Screen_PiTracIRLED]
  Origin = -> Origin
  Type = Assembly
FEATURE [TechDraw::DrawSVGTemplate] Template
  Height = 210
  Orientation = 1
  Template = C:/Program Files/FreeCAD 1.0/data/Mod/TechDraw/Templates/Default_Template_A4_Landscape.svg
  Width = 297
FEATURE [TechDraw::DrawProjGroupItem] View
  CoarseView = false
  Direction = (-0.57735,0.57735,-0.577351)
  Focus = 100
  HardHidden = false
  IsoCount = 0
  IsoHidden = false
  IsoVisible = false
  LockPosition = false
  Perspective = false
  Rotation = 0
  RotationVector = (1,0,0)
  ScaleType = 0
  ScrubCount = 1
  SeamHidden = false
  SeamVisible = false
  SmoothHidden = false
  SmoothVisible = true
  Source = -> [Assembly]
  Type = 0
  X = 148.5
  XDirection = (0.707107,0.707107,0)
  Y = 105
FEATURE [TechDraw::DrawPage] Page
  KeepUpdated = true
  NextBalloonIndex = 1
  ProjectionType = 0
  Template = -> Template
  Views = -> [View]
---- part Assy_Stack_Module_PSU.FCStd = doc fcstd_1510ce4691f9 ----
FCSTD DOCUMENT  (FreeCAD 1.0R39319 (Git))
Label: Assy_Stack_Module_PSU
License: All rights reserved
LicenseURL: https://en.wikipedia.org/wiki/All_rights_reserved
objects: TechDraw::DrawViewBalloon×18, App::Link×17, Part::FeaturePython×8, TechDraw::DrawProjGroupItem×6, TechDraw::DrawViewDimension×4, App::DocumentObjectGroup×3, TechDraw::DrawSVGTemplate×2, TechDraw::DrawPage×2, PartDesign::CoordinateSystem×1, App::FeaturePython×1, Spreadsheet::Sheet×1, TechDraw::DrawViewSpreadsheet×1, TechDraw::DrawViewAnnotation×1, App::Part×1, TechDraw::DrawProjGroup×1
note: 17 computed .brp shape members not serialized (recipe doc carries the construction recipe); baked Part::Feature solids carry a one-line shape summary decoded from their .brp
EXTERNAL_REF file=../../Part/Print/Stack_Module_PSU_vent.FCStd obj=LCS_1
EXTERNAL_REF file=../../Part/Print/Stack_Module_PSU_vent.FCStd obj=Part
EXTERNAL_REF file=Assy_M5_rod.FCStd obj=LCS_Origin
EXTERNAL_REF file=Assy_M5_rod.FCStd obj=Assembly
EXTERNAL_REF file=../../Part/Print/Stack_Module_PSU_vent.FCStd obj=LCS_2
EXTERNAL_REF file=../../Part/Print/Stack_Module_PSU_vent.FCStd obj=LCS_3
EXTERNAL_REF file=../../Part/Print/Stack_Module_PSU_vent.FCStd obj=LCS_4
EXTERNAL_REF file=../../Part/Print/Spacer.FCStd obj=LCS_1
EXTERNAL_REF file=../../Part/Print/Stack_Module_PSU_vent.FCStd obj=spacer_att
EXTERNAL_REF file=../../Part/Print/Spacer.FCStd obj=Part
EXTERNAL_REF file=../../Part/Print/Stack_Module_PSU_vent.FCStd obj=spacer_att_2
EXTERNAL_REF file=../../Part/Print/Stack_Module_PSU_vent.FCStd obj=spacer_att_3
EXTERNAL_REF file=../../Part/Print/Stack_Module_PSU_vent.FCStd obj=spacer_att_004
EXTERNAL_REF file=../../Part/Purchase/LRS-75.FCStd obj=stack_attach
EXTERNAL_REF file=../../Part/Print/Stack_Module_PSU_vent.FCStd obj=PSU_attachment
EXTERNAL_REF file=../../Part/Purchase/LRS-75.FCStd obj=LRS_75_ASM
EXTERNAL_REF file=Assy_Foot.FCStd obj=LCS_Origin
EXTERNAL_REF file=Assy_Foot.FCStd obj=Assembly
EXTERNAL_REF file=../../Part/Print/Ambient_LED_Screen.FCStd obj=stack_att
EXTERNAL_REF file=../../Part/Print/Stack_Module_PSU_vent.FCStd obj=screen_attachment
EXTERNAL_REF file=../../Part/Print/Ambient_LED_Screen.FCStd obj=Part
EXTERNAL_REF file=../../Part/Print/LinePower_Cover.FCStd obj=stack_att
EXTERNAL_REF file=../../Part/Print/Stack_Module_PSU_vent.FCStd obj=linecover_att
EXTERNAL_REF file=../../Part/Print/LinePower_Cover.FCStd obj=Part
EXTERNAL_REF file=../../Part/Print/Ambient_LED_Visor.FCStd obj=LCS_1
EXTERNAL_REF file=../../Part/Print/Ambient_LED_Visor.FCStd obj=Part

FEATURE [App::DocumentObjectGroup] Parts
FEATURE [PartDesign::CoordinateSystem] LCS_Origin
  AttacherType = Attacher::AttachEngine3D
  AttachmentSupport = -> [X_Axis]
  MapMode = 2
FEATURE [App::DocumentObjectGroup] Constraints
FEATURE [App::FeaturePython] Variables  # WARN: FeaturePython — macro-defined, semantics opaque (R4)
  Type = App::PropertyContainer
FEATURE [App::DocumentObjectGroup] Configurations
FEATURE [App::Link] Stack_Module_PSU_vent
  AttachedBy = #LCS_1
  AttachedTo = Parent Assembly#LCS_Origin
  AttachmentOffset = pos=(0,0,0) rot=(-0.57735,-0.57735,0.57735;4.18879rad)
  LinkPlacement = pos=(66.5,3.42e-14,53.5) rot=(0,0,1;3.14159rad)
  LinkedObject = -> <external ../../Part/Print/Stack_Module_PSU_vent.FCStd>#Part
  Placement = pos=(66.5,3.42e-14,53.5) rot=(0,0,1;3.14159rad)
  SolverId = Asm4EE
  expr: Placement = LCS_Origin.Placement * AttachmentOffset * Stack_Module_PSU_vent#LCS_1.Placement ^ -1
FEATURE [App::Link] Assy_M5_rod
  AttachedBy = #LCS_Origin
  AttachedTo = Stack_Module_PSU_vent#LCS_1
  AttachmentOffset = pos=(0,0,2) rot=(1,0,0;3.14159rad)
  LinkPlacement = pos=(1.49e-14,-2,1.47e-14) rot=(0.57735,-0.57735,-0.57735;4.18879rad)
  LinkedObject = -> <external Assy_M5_rod.FCStd>#Assembly
  Placement = pos=(1.49e-14,-2,1.47e-14) rot=(0.57735,-0.57735,-0.57735;4.18879rad)
  SolverId = Asm4EE
  expr: Placement = Stack_Module_PSU_vent.Placement * Stack_Module_PSU_vent#LCS_1.Placement * AttachmentOffset * Assy_M5_rod#LCS_Origin.Placement ^ -1
FEATURE [App::Link] Assy_M5_rod001
  AttachedBy = #LCS_Origin
  AttachedTo = Stack_Module_PSU_vent#LCS_2
  AttachmentOffset = pos=(0,0,2) rot=(1,0,0;3.14159rad)
  LinkPlacement = pos=(3,-2,116) rot=(0.57735,-0.57735,-0.57735;4.18879rad)
  LinkedObject = -> <external Assy_M5_rod.FCStd>#Assembly
  Placement = pos=(3,-2,116) rot=(0.57735,-0.57735,-0.57735;4.18879rad)
  SolverId = Asm4EE
  expr: Placement = Stack_Module_PSU_vent.Placement * Stack_Module_PSU_vent#LCS_2.Placement * AttachmentOffset * Assy_M5_rod#LCS_Origin.Placement ^ -1
FEATURE [App::Link] Assy_M5_rod002
  AttachedBy = #LCS_Origin
  AttachedTo = Stack_Module_PSU_vent#LCS_3
  AttachmentOffset = pos=(0,0,-2) rot=(0,0,1;0rad)
  LinkPlacement = pos=(133,-2,2.89e-14) rot=(-0.57735,0.57735,0.57735;2.0944rad)
  LinkedObject = -> <external Assy_M5_rod.FCStd>#Assembly
  Placement = pos=(133,-2,2.89e-14) rot=(-0.57735,0.57735,0.57735;2.0944rad)
  SolverId = Asm4EE
  expr: Placement = Stack_Module_PSU_vent.Placement * Stack_Module_PSU_vent#LCS_3.Placement * AttachmentOffset * Assy_M5_rod#LCS_Origin.Placement ^ -1
FEATURE [App::Link] Assy_M5_rod003
  AttachedBy = #LCS_Origin
  AttachedTo = Stack_Module_PSU_vent#LCS_4
  AttachmentOffset = pos=(0,0,-2) rot=(0,0,1;0rad)
  LinkPlacement = pos=(130,-2,116) rot=(-0.57735,0.57735,0.57735;2.0944rad)
  LinkedObject = -> <external Assy_M5_rod.FCStd>#Assembly
  Placement = pos=(130,-2,116) rot=(-0.57735,0.57735,0.57735;2.0944rad)
  SolverId = Asm4EE
  expr: Placement = Stack_Module_PSU_vent.Placement * Stack_Module_PSU_vent#LCS_4.Placement * AttachmentOffset * Assy_M5_rod#LCS_Origin.Placement ^ -1
FEATURE [App::Link] Spacer
  AttachedBy = #LCS_1
  AttachedTo = Stack_Module_PSU_vent#spacer_att
  LinkPlacement = pos=(0,35.25,7.1e-15) rot=(0,0.707107,0.707107;3.14159rad)
  LinkedObject = -> <external ../../Part/Print/Spacer.FCStd>#Part
  Placement = pos=(0,35.25,7.1e-15) rot=(0,0.707107,0.707107;3.14159rad)
  SolverId = Asm4EE
  expr: Placement = Stack_Module_PSU_vent.Placement * Stack_Module_PSU_vent#spacer_att.Placement * AttachmentOffset * Spacer#LCS_1.Placement ^ -1
FEATURE [App::Link] Spacer001
  AttachedBy = #LCS_1
  AttachedTo = Stack_Module_PSU_vent#spacer_att_2
  LinkPlacement = pos=(3,35.25,116) rot=(0,0.707107,0.707107;3.14159rad)
  LinkedObject = -> <external ../../Part/Print/Spacer.FCStd>#Part
  Placement = pos=(3,35.25,116) rot=(0,0.707107,0.707107;3.14159rad)
  SolverId = Asm4EE
  expr: Placement = Stack_Module_PSU_vent.Placement * Stack_Module_PSU_vent#spacer_att_2.Placement * AttachmentOffset * Spacer#LCS_1.Placement ^ -1
FEATURE [App::Link] Spacer002
  AttachedBy = #LCS_1
  AttachedTo = Stack_Module_PSU_vent#spacer_att_3
  AttachmentOffset = pos=(0,0,0) rot=(0,1,0;3.14159rad)
  LinkPlacement = pos=(130,35.25,116) rot=(1,0,0;4.71239rad)
  LinkedObject = -> <external ../../Part/Print/Spacer.FCStd>#Part
  Placement = pos=(130,35.25,116) rot=(1,0,0;4.71239rad)
  SolverId = Asm4EE
  expr: Placement = Stack_Module_PSU_vent.Placement * Stack_Module_PSU_vent#spacer_att_3.Placement * AttachmentOffset * Spacer#LCS_1.Placement ^ -1
FEATURE [App::Link] Spacer003
  AttachedBy = #LCS_1
  AttachedTo = Stack_Module_PSU_vent#spacer_att_004
  AttachmentOffset = pos=(0,0,0) rot=(0,1,0;3.14159rad)
  LinkPlacement = pos=(133,35.25,2.13e-14) rot=(1,0,0;4.71239rad)
  LinkedObject = -> <external ../../Part/Print/Spacer.FCStd>#Part
  Placement = pos=(133,35.25,2.13e-14) rot=(1,0,0;4.71239rad)
  SolverId = Asm4EE
  expr: Placement = Stack_Module_PSU_vent.Placement * Stack_Module_PSU_vent#spacer_att_004.Placement * AttachmentOffset * Spacer#LCS_1.Placement ^ -1
FEATURE [App::Link] LRS_75_ASM  label="LRS-75_ASM"
  AttachedBy = #stack_attach
  AttachedTo = Stack_Module_PSU_vent#PSU_attachment
  LinkPlacement = pos=(318.201,10.6,-201.167) rot=(-0.577138,0.577457,0.577457;2.09471rad)
  LinkedObject = -> <external ../../Part/Purchase/LRS-75.FCStd>#LRS_75_ASM
  Placement = pos=(318.201,10.6,-201.167) rot=(-0.577138,0.577457,0.577457;2.09471rad)
  SolverId = Asm4EE
  expr: Placement = Stack_Module_PSU_vent.Placement * Stack_Module_PSU_vent#PSU_attachment.Placement * AttachmentOffset * LRS_75#stack_attach.Placement ^ -1
FEATURE [App::Link] Assy_Foot
  AttachedBy = #LCS_Origin
  AttachedTo = Stack_Module_PSU_vent#LCS_1
  AttachmentOffset = pos=(0,0,5) rot=(0,1,0;3.14159rad)
  LinkPlacement = pos=(1.59e-14,-5,1.53e-14) rot=(0.57735,0.57735,0.57735;4.18879rad)
  LinkedObject = -> <external Assy_Foot.FCStd>#Assembly
  Placement = pos=(1.59e-14,-5,1.53e-14) rot=(0.57735,0.57735,0.57735;4.18879rad)
  SolverId = Asm4EE
  expr: Placement = Stack_Module_PSU_vent.Placement * Stack_Module_PSU_vent#LCS_1.Placement * AttachmentOffset * Assy_Foot#LCS_Origin.Placement ^ -1
FEATURE [App::Link] Assy_Foot001
  AttachedBy = #LCS_Origin
  AttachedTo = Stack_Module_PSU_vent#LCS_2
  AttachmentOffset = pos=(0,0,5) rot=(0,1,0;3.14159rad)
  LinkPlacement = pos=(3,-5,116) rot=(0.57735,0.57735,0.57735;4.18879rad)
  LinkedObject = -> <external Assy_Foot.FCStd>#Assembly
  Placement = pos=(3,-5,116) rot=(0.57735,0.57735,0.57735;4.18879rad)
  SolverId = Asm4EE
  expr: Placement = Stack_Module_PSU_vent.Placement * Stack_Module_PSU_vent#LCS_2.Placement * AttachmentOffset * Assy_Foot#LCS_Origin.Placement ^ -1
FEATURE [App::Link] Assy_Foot002
  AttachedBy = #LCS_Origin
  AttachedTo = Stack_Module_PSU_vent#LCS_3
  AttachmentOffset = pos=(0,0,-5) rot=(0,0,1;0rad)
  LinkPlacement = pos=(133,-5,2.95e-14) rot=(-0.57735,0.57735,0.57735;2.0944rad)
  LinkedObject = -> <external Assy_Foot.FCStd>#Assembly
  Placement = pos=(133,-5,2.95e-14) rot=(-0.57735,0.57735,0.57735;2.0944rad)
  SolverId = Asm4EE
  expr: Placement = Stack_Module_PSU_vent.Placement * Stack_Module_PSU_vent#LCS_3.Placement * AttachmentOffset * Assy_Foot#LCS_Origin.Placement ^ -1
FEATURE [App::Link] Assy_Foot003
  AttachedBy = #LCS_Origin
  AttachedTo = Stack_Module_PSU_vent#LCS_4
  AttachmentOffset = pos=(0,0,-5) rot=(0,0,1;0rad)
  LinkPlacement = pos=(130,-5,116) rot=(-0.57735,0.57735,0.57735;2.0944rad)
  LinkedObject = -> <external Assy_Foot.FCStd>#Assembly
  Placement = pos=(130,-5,116) rot=(-0.57735,0.57735,0.57735;2.0944rad)
  SolverId = Asm4EE
  expr: Placement = Stack_Module_PSU_vent.Placement * Stack_Module_PSU_vent#LCS_4.Placement * AttachmentOffset * Assy_Foot#LCS_Origin.Placement ^ -1
FEATURE [App::Link] Ambient_LED_Screen
  AttachedBy = #stack_att
  AttachedTo = Stack_Module_PSU_vent#screen_attachment
  LinkPlacement = pos=(66.5,3,-9) rot=(1,0,0;4.71239rad)
  LinkedObject = -> <external ../../Part/Print/Ambient_LED_Screen.FCStd>#Part
  Placement = pos=(66.5,3,-9) rot=(1,0,0;4.71239rad)
  SolverId = Asm4EE
  expr: Placement = Stack_Module_PSU_vent.Placement * Stack_Module_PSU_vent#screen_attachment.Placement * AttachmentOffset * Ambient_LED_Screen#stack_att.Placement ^ -1
FEATURE [App::Link] LinePower_Cover
  AttachedBy = #stack_att
  AttachedTo = Stack_Module_PSU_vent#linecover_att
  AttachmentOffset = pos=(0,0,0) rot=(0,0,1;3.14159rad)
  LinkPlacement = pos=(10.5,4,120.5) rot=(1,0,0;4.71239rad)
  LinkedObject = -> <external ../../Part/Print/LinePower_Cover.FCStd>#Part
  Placement = pos=(10.5,4,120.5) rot=(1,0,0;4.71239rad)
  SolverId = Asm4EE
  expr: Placement = Stack_Module_PSU_vent.Placement * Stack_Module_PSU_vent#linecover_att.Placement * AttachmentOffset * LinePower_Cover#stack_att.Placement ^ -1
FEATURE [Part::FeaturePython] Screw  label="ST2.9x6.5-Screw013"  # WARN: FeaturePython — macro-defined, semantics opaque (R4)
  BaseObject = -> Stack_Module_PSU_vent [Body.LinearPattern005.Edge4238]
  Diameter = 2
  Invert = false
  LeftHanded = false
  Length = 0
  LengthCustom = 6.5
  MatchOuter = false
  Offset = 2
  OffsetAngle = 0
  Placement = pos=(108.5,6,1.5) rot=(-1,0,0;1.5708rad)
  Thread = false
  Type = 81
FEATURE [Part::FeaturePython] Screw002  label="ST2.9x6.5-Screw"  # WARN: FeaturePython — macro-defined, semantics opaque (R4)
  BaseObject = -> Stack_Module_PSU_vent [Body.LinearPattern005.Edge4103]
  Diameter = 2
  Invert = false
  LeftHanded = false
  Length = 0
  LengthCustom = 6.5
  MatchOuter = false
  Offset = 2
  OffsetAngle = 0
  Placement = pos=(23.5,6,94) rot=(-1,0,0;1.5708rad)
  Thread = false
  Type = 81
FEATURE [Part::FeaturePython] Screw003  label="ST2.9x6.5-Screw014"  # WARN: FeaturePython — macro-defined, semantics opaque (R4)
  BaseObject = -> LinePower_Cover [Body.Fillet007.Edge85]
  Diameter = 2
  Invert = false
  LeftHanded = false
  Length = 0
  LengthCustom = 6.5
  MatchOuter = false
  OffsetAngle = 0
  Placement = pos=(53.5,10,116.5) rot=(-1,0,0;1.5708rad)
  Thread = false
  Type = 81
FEATURE [Part::FeaturePython] Screw004  label="ST2.9x6.5-Screw015"  # WARN: FeaturePython — macro-defined, semantics opaque (R4)
  BaseObject = -> LinePower_Cover [Body.Fillet007.Edge96]
  Diameter = 2
  Invert = false
  LeftHanded = false
  Length = 0
  LengthCustom = 6.5
  MatchOuter = false
  OffsetAngle = 0
  Placement = pos=(13.5,10,84.5) rot=(-1,0,0;1.5708rad)
  Thread = false
  Type = 81
FEATURE [Part::FeaturePython] Screw005  label="M3x6-Screw"  # WARN: FeaturePython — macro-defined, semantics opaque (R4)
  BaseObject = -> Stack_Module_PSU_vent [Body.LinearPattern005.Edge1214]
  Diameter = 1
  Invert = true
  LeftHanded = false
  Length = 1
  LengthCustom = 6
  MatchOuter = false
  OffsetAngle = 0
  Placement = pos=(69.5,2.01e-14,23) rot=(1,0,0;1.5708rad)
  Thread = false
  Type = 37
FEATURE [Part::FeaturePython] Screw006  label="M3x6-Screw001"  # WARN: FeaturePython — macro-defined, semantics opaque (R4)
  BaseObject = -> Stack_Module_PSU_vent [Body.LinearPattern005.Edge1213]
  Diameter = 1
  Invert = true
  LeftHanded = false
  Length = 1
  LengthCustom = 6
  MatchOuter = false
  OffsetAngle = 0
  Placement = pos=(69.5,4.1e-14,78) rot=(1,0,0;1.5708rad)
  Thread = false
  Type = 37
FEATURE [Part::FeaturePython] Screw007  label="ST2.9x9.5-Screw"  # WARN: FeaturePython — macro-defined, semantics opaque (R4)
  BaseObject = -> Stack_Module_PSU_vent [Body.LinearPattern005.Edge1216]
  Diameter = 2
  Invert = false
  LeftHanded = false
  Length = 1
  LengthCustom = 9.5
  MatchOuter = false
  OffsetAngle = 0
  Placement = pos=(127,2.26e-14,-12) rot=(1,0,0;1.5708rad)
  Thread = false
  Type = 81
FEATURE [Part::FeaturePython] Screw008  label="ST2.9x9.5-Screw001"  # WARN: FeaturePython — macro-defined, semantics opaque (R4)
  BaseObject = -> Stack_Module_PSU_vent [Body.LinearPattern005.Edge1215]
  Diameter = 2
  Invert = true
  LeftHanded = false
  Length = 1
  LengthCustom = 9.5
  MatchOuter = false
  OffsetAngle = 0
  Placement = pos=(6,-1.77e-14,-12) rot=(1,0,0;1.5708rad)
  Thread = false
  Type = 81
FEATURE [Spreadsheet::Sheet] Spreadsheet  label="BOM"
  cells = A1=12; B1=4; C1='M3x10 mm self-tapping screw; D1=' 5-16 mm; A2=11; B2=4; C2='M3x5 mm self-tapping screw; D2='5-6 mm; A3=10; B3=2; C3='M3x6 mm screw; D3='5-6 mm; A4=9; B4=3; C4='Wires; D4='-; A5=8; B5=1; C5='USB COB LED Strip Lights; D5='roughly 60 cm; A6=7; B6=1; C6='AC Power Inlet C14 with Fuse; D6='-; A7=6; B7=1; C7='Meanwell LRS-75-5; D7='-; A8=5; B8=4; C8='Spacer; D8='-; E8='PETG or PLA; A9=4; B9=1; C9='Ambient_LED_Visor; D9='-; E9='PETG or PLA; A10=3; B10=1; C10='LinePower_Cover; D10='-; E10='PETG or PLA; A11=2; B11=1; C11='Ambient_LED_Screen; D11='-; E11='PETG or PLA; A12=1; B12=1; C12='Stack_Module_PSU_vent; D12='-; E12='PETG or PLA; A13='Position; B13='Quantity; C13='Part; D13='Dimensions; E13='Material
FEATURE [TechDraw::DrawViewBalloon] Balloon
  BubbleShape = 0
  EndType = 0
  EndTypeScale = 1
  KinkLength = 5
  LockPosition = false
  OriginX = 74.9138
  OriginY = -16.347
  Rotation = 0
  ScaleType = 0
  ShapeScale = 1
  Text = 1
  TextWrapLen = -1
  X = 128.799
  Y = -72.3092
FEATURE [TechDraw::DrawViewBalloon] Balloon003
  BubbleShape = 0
  EndType = 0
  EndTypeScale = 1
  KinkLength = 5
  LockPosition = false
  OriginX = -3.65673
  OriginY = -43.3871
  Rotation = 0
  ScaleType = 0
  ShapeScale = 1
  Text = 4
  TextWrapLen = -1
  X = 130.81
  Y = -93.7522
FEATURE [TechDraw::DrawSVGTemplate] Template001
  EditableTexts = approval_person=GitHubPR; creator=Stefan; date_of_issue=19/3/2026; document_type=Assy_Stack_Module_PSU; general_tolerances=na; identification_number=na; language_code=EN; part_material=na; revision_index=AAA; scale=1 : 1; sheet_number=1 / 1; title=Assy_Stack_Module_PSU
  Height = 420
  Orientation = 1
  Template = <userpath>/Documents/PiTrac/3D Printed Parts/Enclosure Version 3/Assets/PiTrac_A2_Landscape_ISO5457_minimal.svg
  Width = 594
FEATURE [TechDraw::DrawViewSpreadsheet] Sheet001
  CellEnd = E13
  CellStart = A1
  Font = osifont
  LineWidth = 0.35
  LockPosition = false
  Rotation = 0
  ScaleType = 2
  Source = -> Spreadsheet
  Symbol = <blob: 14232 chars omitted>
  TextSize = 12
  X = 502.594
  Y = 129.653
FEATURE [TechDraw::DrawViewAnnotation] Annotation
  Font = osifont
  LineSpace = 100
  LockPosition = false
  MaxWidth = -1
  Rotation = 0
  ScaleType = 0
  Text = Not all parts are shown
  TextSize = 5
  TextStyle = 0
  X = 341.029
  Y = 39.0208
FEATURE [App::Link] Ambient_LED_Visor
  AttachedBy = #LCS_1
  AttachedTo = Parent Assembly#LCS_Origin
  AttachmentOffset = pos=(66.5,0,-46.5) rot=(0,0,1;3.14159rad)
  LinkPlacement = pos=(66.5,0,-46.5) rot=(0,0,1;3.14159rad)
  LinkedObject = -> <external ../../Part/Print/Ambient_LED_Visor.FCStd>#Part
  Placement = pos=(66.5,0,-46.5) rot=(0,0,1;3.14159rad)
  SolverId = Asm4EE
  expr: Placement = LCS_Origin.Placement * AttachmentOffset * Ambient_LED_Visor#LCS_1.Placement ^ -1
FEATURE [App::Part] Assembly  label="Assy_Stack_Module_PSU"
  AssemblyType = Part::Link
  Group = -> [LCS_Origin,Constraints,Variables,Configurations,Stack_Module_PSU_vent,Assy_M5_rod,Assy_M5_rod001,Assy_M5_rod002,Assy_M5_rod003,Spacer,Spacer001,Spacer002,Spacer003,LRS_75_ASM,Assy_Foot,Assy_Foot001,Assy_Foot002,Assy_Foot003,Ambient_LED_Screen,LinePower_Cover,Screw,Screw002,Screw003,Screw004,Screw005,Screw006,Screw007,Screw008,Ambient_LED_Visor]
  Origin = -> Origin
  Type = Assembly
FEATURE [TechDraw::DrawProjGroupItem] ProjItem  label="Top"
  CoarseView = false
  Direction = (0,1,0)
  Focus = 100
  HardHidden = false
  IsoCount = 0
  IsoHidden = false
  IsoVisible = false
  LockPosition = false
  Perspective = false
  Rotation = 0
  RotationVector = (1,0,0)
  ScaleType = 0
  ScrubCount = 1
  SeamHidden = false
  SeamVisible = false
  SmoothHidden = false
  SmoothVisible = true
  Source = -> [Assembly]
  Type = 4
  X = 0
  XDirection = (-1,0,-2e-16)
  Y = -133.625
FEATURE [TechDraw::DrawProjGroupItem] View002  label="Isometric View Scale 1:2"
  CoarseView = false
  Direction = (-0.57735,0.57735,-0.57735)
  Focus = 100
  HardHidden = false
  IsoCount = 0
  IsoHidden = false
  IsoVisible = false
  LockPosition = false
  Perspective = false
  Rotation = 0
  RotationVector = (1,0,0)
  Scale = 0.5
  ScaleType = 2
  ScrubCount = 1
  SeamHidden = false
  SeamVisible = false
  SmoothHidden = false
  SmoothVisible = true
  Source = -> [Assembly]
  Type = 0
  X = 336.894
  XDirection = (-0.707106,0,0.707106)
  Y = 114.331
FEATURE [TechDraw::DrawProjGroupItem] View003  label="Front001"
  CoarseView = false
  Direction = (0,0,-1)
  Focus = 100
  HardHidden = false
  IsoCount = 0
  IsoHidden = false
  IsoVisible = false
  LockPosition = true
  Perspective = false
  Rotation = 0
  RotationVector = (1,0,0)
  ScaleType = 2
  ScrubCount = 1
  SeamHidden = false
  SeamVisible = false
  SmoothHidden = false
  SmoothVisible = true
  Source = -> [Assembly]
  Type = 0
  X = 0
  XDirection = (-1,0,0)
  Y = 0
FEATURE [TechDraw::DrawProjGroupItem] ProjItem002  label="Top001"
  CoarseView = false
  Direction = (0,1,0)
  Focus = 100
  HardHidden = false
  IsoCount = 0
  IsoHidden = false
  IsoVisible = false
  LockPosition = false
  Perspective = false
  Rotation = 0
  RotationVector = (1,0,0)
  ScaleType = 0
  ScrubCount = 1
  SeamHidden = false
  SeamVisible = false
  SmoothHidden = false
  SmoothVisible = true
  Source = -> [Assembly]
  Type = 4
  X = 0
  XDirection = (-1,0,0)
  Y = -132.298
FEATURE [TechDraw::DrawProjGroupItem] ProjItem003  label="Left001"
  CoarseView = false
  Direction = (1,0,-1e-16)
  Focus = 100
  HardHidden = false
  IsoCount = 0
  IsoHidden = false
  IsoVisible = false
  LockPosition = false
  Perspective = false
  Rotation = 0
  RotationVector = (1,0,0)
  ScaleType = 0
  ScrubCount = 1
  SeamHidden = false
  SeamVisible = false
  SmoothHidden = false
  SmoothVisible = true
  Source = -> [Assembly]
  Type = 1
  X = 187
  XDirection = (-1e-16,0,-1)
  Y = 0
FEATURE [TechDraw::DrawProjGroup] ProjGroup001
  Anchor = -> View003
  AutoDistribute = true
  LockPosition = false
  ProjectionType = 0
  Rotation = 0
  ScaleType = 0
  Source = -> [Assembly]
  Views = -> [View003,ProjItem002,ProjItem003]
  X = 154.029
  Y = 330.521
  spacingX = 15
  spacingY = 15
FEATURE [TechDraw::DrawViewBalloon] Balloon007
  BubbleShape = 0
  EndType = 0
  EndTypeScale = 1
  KinkLength = 5
  LockPosition = false
  OriginX = -59
  OriginY = 9.65153
  Rotation = 0
  ScaleType = 0
  ShapeScale = 1
  SourceView = -> ProjItem002
  Text = 1
  TextWrapLen = -1
  X = -100
  Y = 25.036
FEATURE [TechDraw::DrawViewBalloon] Balloon008
  BubbleShape = 0
  EndType = 0
  EndTypeScale = 1
  KinkLength = 5
  LockPosition = false
  OriginX = -39.6652
  OriginY = 0.173159
  Rotation = 0
  ScaleType = 0
  ShapeScale = 1
  SourceView = -> View003
  Text = 2
  TextWrapLen = -1
  X = -100
  Y = 15.5576
FEATURE [TechDraw::DrawViewBalloon] Balloon009
  BubbleShape = 0
  EndType = 0
  EndTypeScale = 1
  KinkLength = 5
  LockPosition = false
  OriginX = 32.6431
  OriginY = 50.5032
  Rotation = 0
  ScaleType = 0
  ShapeScale = 1
  SourceView = -> ProjItem002
  Text = 3
  TextWrapLen = -1
  X = 100
  Y = 58.1951
FEATURE [TechDraw::DrawViewBalloon] Balloon010
  BubbleShape = 0
  EndType = 0
  EndTypeScale = 1
  KinkLength = 5
  LockPosition = false
  OriginX = -44.7952
  OriginY = -78.7316
  Rotation = 0
  ScaleType = 0
  ShapeScale = 1
  SourceView = -> ProjItem002
  Text = 4
  TextWrapLen = -1
  X = -100
  Y = -60.2701
FEATURE [TechDraw::DrawViewBalloon] Balloon011
  BubbleShape = 0
  EndType = 0
  EndTypeScale = 1
  KinkLength = 5
  LockPosition = false
  OriginX = -63.25
  OriginY = -48.5
  Rotation = 0
  ScaleType = 0
  ShapeScale = 1
  SourceView = -> ProjItem002
  Text = 5
  TextWrapLen = -1
  X = -100
  Y = -23.3716
FEATURE [TechDraw::DrawViewBalloon] Balloon012
  BubbleShape = 0
  EndType = 0
  EndTypeScale = 1
  KinkLength = 5
  LockPosition = false
  OriginX = -59.1546
  OriginY = 67.9396
  Rotation = 0
  ScaleType = 0
  ShapeScale = 1
  SourceView = -> ProjItem002
  Text = 5
  TextWrapLen = -1
  X = -100
  Y = 85
FEATURE [TechDraw::DrawViewBalloon] Balloon014
  BubbleShape = 0
  EndType = 0
  EndTypeScale = 1
  KinkLength = 5
  LockPosition = false
  OriginX = 62.9004
  OriginY = 64.8626
  Rotation = 0
  ScaleType = 0
  ShapeScale = 1
  SourceView = -> ProjItem002
  Text = 5
  TextWrapLen = -1
  X = 99.4872
  Y = 83.9743
FEATURE [TechDraw::DrawViewBalloon] Balloon015
  BubbleShape = 0
  EndType = 0
  EndTypeScale = 1
  KinkLength = 5
  LockPosition = false
  OriginX = 64.4389
  OriginY = -46.4229
  Rotation = 0
  ScaleType = 0
  ShapeScale = 1
  SourceView = -> ProjItem002
  Text = 5
  TextWrapLen = -1
  X = 100
  Y = -30.5256
FEATURE [TechDraw::DrawViewBalloon] Balloon016
  BubbleShape = 0
  EndType = 0
  EndTypeScale = 1
  KinkLength = 5
  LockPosition = false
  OriginX = 19.8222
  OriginY = 26.3999
  Rotation = 0
  ScaleType = 0
  ShapeScale = 1
  SourceView = -> ProjItem002
  Text = 6
  TextWrapLen = -1
  X = 100
  Y = 14.604
FEATURE [TechDraw::DrawViewBalloon] Balloon017
  BubbleShape = 0
  EndType = 0
  EndTypeScale = 1
  KinkLength = 5
  LockPosition = false
  OriginX = -26.75
  OriginY = -21.6518
  Rotation = 0
  ScaleType = 0
  ShapeScale = 1
  SourceView = -> ProjItem003
  Text = 10
  TextWrapLen = -1
  X = -42.1357
  Y = -49
FEATURE [TechDraw::DrawViewBalloon] Balloon018
  BubbleShape = 0
  EndType = 0
  EndTypeScale = 1
  KinkLength = 5
  LockPosition = false
  OriginX = 28.7257
  OriginY = -22.306
  Rotation = 0
  ScaleType = 0
  ShapeScale = 1
  SourceView = -> ProjItem003
  Text = 10
  TextWrapLen = -1
  X = 47.7
  Y = -49
FEATURE [TechDraw::DrawViewBalloon] Balloon019
  BubbleShape = 0
  EndType = 0
  EndTypeScale = 1
  KinkLength = 5
  LockPosition = false
  OriginX = -61.2512
  OriginY = -22.105
  Rotation = 0
  ScaleType = 0
  ShapeScale = 1
  SourceView = -> View003
  Text = 12
  TextWrapLen = -1
  X = -100
  Y = -14.4131
FEATURE [TechDraw::DrawViewBalloon] Balloon020
  BubbleShape = 0
  EndType = 0
  EndTypeScale = 1
  KinkLength = 5
  LockPosition = false
  OriginX = 61.2512
  OriginY = -22.105
  Rotation = 0
  ScaleType = 0
  ShapeScale = 1
  SourceView = -> View003
  Text = 12
  TextWrapLen = -1
  X = 122.791
  Y = -49
FEATURE [TechDraw::DrawViewBalloon] Balloon021
  BubbleShape = 0
  EndType = 0
  EndTypeScale = 1
  KinkLength = 5
  LockPosition = false
  OriginX = 12.4289
  OriginY = 67.795
  Rotation = 0
  ScaleType = 0
  ShapeScale = 1
  SourceView = -> ProjItem002
  Text = 11
  TextWrapLen = -1
  X = -100
  Y = 101.947
FEATURE [TechDraw::DrawViewBalloon] Balloon022
  BubbleShape = 0
  EndType = 0
  EndTypeScale = 1
  KinkLength = 5
  LockPosition = false
  OriginX = 53.6694
  OriginY = 36.1438
  Rotation = 0
  ScaleType = 0
  ShapeScale = 1
  SourceView = -> ProjItem002
  Text = 11
  TextWrapLen = -1
  X = 100
  Y = 36.7508
FEATURE [TechDraw::DrawViewBalloon] Balloon024
  BubbleShape = 0
  EndType = 0
  EndTypeScale = 1
  KinkLength = 5
  LockPosition = false
  OriginX = -40.504
  OriginY = -48.9784
  Rotation = 0
  ScaleType = 0
  ShapeScale = 1
  SourceView = -> ProjItem002
  Text = 11
  TextWrapLen = -1
  X = -100
  Y = -0.151091
FEATURE [TechDraw::DrawViewDimension] Dimension001
  AngleOverride = false
  Arbitrary = false
  ArbitraryTolerances = false
  BoxCorners = (2) [(-95,-22.2982,-1e-07),(95,22.2982,1e-07)]
  EqualTolerance = true
  ExtensionAngle = 0
  FormatSpec = %.2w
  FormatSpecOverTolerance = %+.2w
  FormatSpecUnderTolerance = %+.2w
  Inverted = false
  LineAngle = 0
  LockPosition = false
  MeasureType = 1
  OverTolerance = 0
  References2D = -> [ProjItem003]
  Rotation = 0
  ScaleType = 0
  TheoreticalExact = false
  Type = 1
  UnderTolerance = 0
  X = 0
  Y = 40
FEATURE [TechDraw::DrawViewDimension] Dimension002
  AngleOverride = false
  Arbitrary = false
  ArbitraryTolerances = false
  BoxCorners = (2) [(-77,-22.2982,-1e-07),(77,22.2982,1e-07)]
  EqualTolerance = true
  ExtensionAngle = 0
  FormatSpec = %.2w
  FormatSpecOverTolerance = %+.2w
  FormatSpecUnderTolerance = %+.2w
  Inverted = false
  LineAngle = 0
  LockPosition = false
  MeasureType = 1
  OverTolerance = 0
  References2D = -> [View003]
  Rotation = 0
  ScaleType = 0
  TheoreticalExact = false
  Type = 1
  UnderTolerance = 0
  X = 0
  Y = 40
FEATURE [TechDraw::DrawViewDimension] Dimension003
  AngleOverride = false
  Arbitrary = false
  ArbitraryTolerances = false
  BoxCorners = (2) [(-95,-22.2982,-1e-07),(95,22.2982,1e-07)]
  EqualTolerance = true
  ExtensionAngle = 0
  FormatSpec = %.2w
  FormatSpecOverTolerance = %+.2w
  FormatSpecUnderTolerance = %+.2w
  Inverted = false
  LineAngle = 0
  LockPosition = false
  MeasureType = 1
  OverTolerance = 0
  References2D = -> [ProjItem003]
  Rotation = 0
  ScaleType = 0
  TheoreticalExact = false
  Type = 0
  UnderTolerance = 0
  X = 131.873
  Y = 0.173159
FEATURE [TechDraw::DrawViewDimension] Dimension004
  AngleOverride = false
  Arbitrary = false
  ArbitraryTolerances = false
  BoxCorners = (2) [(-95,-22.2982,-1e-07),(95,22.2982,1e-07)]
  EqualTolerance = true
  ExtensionAngle = 0
  FormatSpec = %.2w
  FormatSpecOverTolerance = %+.2w
  FormatSpecUnderTolerance = %+.2w
  Inverted = false
  LineAngle = 0
  LockPosition = false
  MeasureType = 1
  OverTolerance = 0
  References2D = -> [ProjItem003]
  Rotation = 0
  ScaleType = 0
  TheoreticalExact = false
  Type = 2
  UnderTolerance = 0
  X = 160.232
  Y = 0.323159
FEATURE [TechDraw::DrawPage] Page001
  KeepUpdated = true
  NextBalloonIndex = 21
  ProjectionType = 0
  Template = -> Template001
  Views = -> [View002,Sheet001,ProjGroup001,Balloon007,Balloon008,Balloon009,Balloon010,Balloon011,Balloon012,Balloon014,Balloon015,Balloon016,Balloon017,Balloon018,Balloon019,Balloon020,Balloon021,Balloon022,Balloon024,Dimension001,Dimension002,Dimension003,Dimension004,Annotation]
FEATURE [TechDraw::DrawSVGTemplate] Template
  Height = 210
  Orientation = 1
  Template = C:/Program Files/FreeCAD 1.0/data/Mod/TechDraw/Templates/Default_Template_A4_Landscape.svg
  Width = 297
FEATURE [TechDraw::DrawProjGroupItem] View
  CoarseView = false
  Direction = (-0.57735,0.57735,-0.57735)
  Focus = 100
  HardHidden = false
  IsoCount = 0
  IsoHidden = false
  IsoVisible = false
  LockPosition = false
  Perspective = false
  Rotation = 0
  RotationVector = (1,0,0)
  ScaleType = 0
  ScrubCount = 1
  SeamHidden = false
  SeamVisible = false
  SmoothHidden = false
  SmoothVisible = true
  Source = -> [Assembly]
  Type = 0
  X = 148.5
  XDirection = (-0.707106,0,0.707106)
  Y = 105
FEATURE [TechDraw::DrawPage] Page
  KeepUpdated = true
  NextBalloonIndex = 1
  ProjectionType = 0
  Template = -> Template
  Views = -> [View]
---- part Assy_Stack_Module_Tee_Cam.FCStd = doc fcstd_4e97c33d2e80 ----
FCSTD DOCUMENT  (FreeCAD 1.0R39319 (Git))
Label: Assy_Stack_Module_Tee_Cam
License: All rights reserved
LicenseURL: https://en.wikipedia.org/wiki/All_rights_reserved
objects: App::DocumentObjectGroup×3, App::Link×2, PartDesign::CoordinateSystem×1, App::FeaturePython×1, App::Part×1, TechDraw::DrawSVGTemplate×1, TechDraw::DrawProjGroupItem×1, TechDraw::DrawPage×1
note: 1 computed .brp shape members not serialized (recipe doc carries the construction recipe); baked Part::Feature solids carry a one-line shape summary decoded from their .brp
EXTERNAL_REF file=Assy_Stack_Module.FCStd obj=LCS_Origin
EXTERNAL_REF file=Assy_Stack_Module.FCStd obj=Assembly
EXTERNAL_REF file=Assy_Tee_Cam.FCStd obj=LCS_Origin
EXTERNAL_REF file=Assy_Tee_Cam.FCStd obj=Assembly

FEATURE [App::DocumentObjectGroup] Parts
FEATURE [PartDesign::CoordinateSystem] LCS_Origin
  AttacherType = Attacher::AttachEngine3D
  AttachmentSupport = -> [X_Axis]
  MapMode = 2
FEATURE [App::DocumentObjectGroup] Constraints
FEATURE [App::FeaturePython] Variables  # WARN: FeaturePython — macro-defined, semantics opaque (R4)
  Type = App::PropertyContainer
FEATURE [App::DocumentObjectGroup] Configurations
FEATURE [App::Link] Assy_Stack_Module
  AttachedBy = #LCS_Origin
  AttachedTo = Parent Assembly#LCS_Origin
  LinkedObject = -> <external Assy_Stack_Module.FCStd>#Assembly
  SolverId = Asm4EE
  expr: Placement = LCS_Origin.Placement * AttachmentOffset * Assy_Stack_Module#LCS_Origin.Placement ^ -1
FEATURE [App::Link] Assy_Tee_Cam
  AttachedBy = #LCS_Origin
  AttachedTo = Assy_Stack_Module#LCS_Origin
  AttachmentOffset = pos=(0,50,-41.75) rot=(-0.57735,0.57735,-0.57735;4.18879rad)
  LinkPlacement = pos=(0,50,-41.75) rot=(-0.57735,0.57735,-0.57735;4.18879rad)
  LinkedObject = -> <external Assy_Tee_Cam.FCStd>#Assembly
  Placement = pos=(0,50,-41.75) rot=(-0.57735,0.57735,-0.57735;4.18879rad)
  SolverId = Asm4EE
  expr: Placement = Assy_Stack_Module.Placement * Assy_Stack_Module#LCS_Origin.Placement * AttachmentOffset * Assy_Tee_Cam#LCS_Origin.Placement ^ -1
FEATURE [App::Part] Assembly  label="Assy_Stack_Module_Tee_Cam"
  AssemblyType = Part::Link
  Group = -> [LCS_Origin,Constraints,Variables,Configurations,Assy_Stack_Module,Assy_Tee_Cam]
  Origin = -> Origin
  Type = Assembly
FEATURE [TechDraw::DrawSVGTemplate] Template
  Height = 210
  Orientation = 1
  Template = C:/Program Files/FreeCAD 1.0/data/Mod/TechDraw/Templates/Default_Template_A4_Landscape.svg
  Width = 297
FEATURE [TechDraw::DrawProjGroupItem] View
  CoarseView = false
  Direction = (-0.57735,0.57735,-0.577351)
  Focus = 100
  HardHidden = false
  IsoCount = 0
  IsoHidden = false
  IsoVisible = false
  LockPosition = false
  Perspective = false
  Rotation = 0
  RotationVector = (1,0,0)
  ScaleType = 0
  ScrubCount = 1
  SeamHidden = false
  SeamVisible = false
  SmoothHidden = false
  SmoothVisible = true
  Source = -> [Assembly]
  Type = 0
  X = 148.5
  XDirection = (0.707107,0.707107,0)
  Y = 105
FEATURE [TechDraw::DrawPage] Page
  KeepUpdated = true
  NextBalloonIndex = 1
  ProjectionType = 0
  Template = -> Template
  Views = -> [View]
---- part Assy_V3Connector_Board.FCStd = doc fcstd_e3913032e6b3 ----
FCSTD DOCUMENT  (FreeCAD 1.0R39319 (Git))
Label: Assy_V3Connector_Board
License: All rights reserved
LicenseURL: https://en.wikipedia.org/wiki/All_rights_reserved
objects: TechDraw::DrawViewBalloon×6, Part::FeaturePython×4, TechDraw::DrawProjGroupItem×4, App::DocumentObjectGroup×3, TechDraw::DrawViewDimension×3, App::Link×2, TechDraw::DrawSVGTemplate×2, TechDraw::DrawPage×2, PartDesign::CoordinateSystem×1, App::FeaturePython×1, App::Part×1, Spreadsheet::Sheet×1, TechDraw::DrawViewSpreadsheet×1, TechDraw::DrawProjGroup×1
note: 11 computed .brp shape members not serialized (recipe doc carries the construction recipe); baked Part::Feature solids carry a one-line shape summary decoded from their .brp
EXTERNAL_REF file=../../Part/Print/ConnectorBoardv3_Carrier.FCStd obj=LCS_1
EXTERNAL_REF file=../../Part/Print/ConnectorBoardv3_Carrier.FCStd obj=Part
EXTERNAL_REF file=../../Part/Print/ConnectorBoardv3_Carrier.FCStd obj=LCS_2
EXTERNAL_REF file=../../Part/Purchase/V3_Connector_board.FCStd obj=LCS_1
EXTERNAL_REF file=../../Part/Purchase/V3_Connector_board.FCStd obj=V3_Connector_Only_1

FEATURE [App::DocumentObjectGroup] Parts
FEATURE [PartDesign::CoordinateSystem] LCS_Origin
  AttacherType = Attacher::AttachEngine3D
  AttachmentSupport = -> [X_Axis]
  MapMode = 2
FEATURE [App::DocumentObjectGroup] Constraints
FEATURE [App::FeaturePython] Variables  # WARN: FeaturePython — macro-defined, semantics opaque (R4)
  Type = App::PropertyContainer
FEATURE [App::DocumentObjectGroup] Configurations
FEATURE [App::Link] ConnectorBoardv3_Carrier
  AttachedBy = #LCS_1
  AttachedTo = Parent Assembly#LCS_Origin
  LinkedObject = -> <external ../../Part/Print/ConnectorBoardv3_Carrier.FCStd>#Part
  SolverId = Asm4EE
  expr: Placement = LCS_Origin.Placement * AttachmentOffset * ConnectorBoardv3_Carrier#LCS_1.Placement ^ -1
FEATURE [App::Link] V3_Connector_Only_1  label="V3 Connector Only 1"
  AttachedBy = #LCS_1
  AttachedTo = ConnectorBoardv3_Carrier#LCS_2
  AttachmentOffset = pos=(0,0,0) rot=(0.707107,-0.707107,0;3.14159rad)
  LinkPlacement = pos=(-50.0123,-11.5506,-30.0106) rot=(-0.57735,0.57735,-0.57735;4.18879rad)
  LinkedObject = -> <external ../../Part/Purchase/V3_Connector_board.FCStd>#V3_Connector_Only_1
  Placement = pos=(-50.0123,-11.5506,-30.0106) rot=(-0.57735,0.57735,-0.57735;4.18879rad)
  SolverId = Asm4EE
  expr: Placement = ConnectorBoardv3_Carrier.Placement * ConnectorBoardv3_Carrier#LCS_2.Placement * AttachmentOffset * V3_Connector_board#LCS_1.Placement ^ -1
FEATURE [Part::FeaturePython] Screw  label="ST2.9x9.5-Screw"  # WARN: FeaturePython — macro-defined, semantics opaque (R4)
  BaseObject = -> V3_Connector_Only_1 [Part__Feature388.Edge261]
  Diameter = 2
  Invert = false
  LeftHanded = false
  Length = 1
  LengthCustom = 9.5
  MatchOuter = false
  OffsetAngle = 0
  Placement = pos=(-44,-12.3124,-24) rot=(1,0,0;1.5708rad)
  Thread = false
  Type = 81
FEATURE [Part::FeaturePython] Screw001  label="ST2.9x9.5-Screw004"  # WARN: FeaturePython — macro-defined, semantics opaque (R4)
  BaseObject = -> V3_Connector_Only_1 [Part__Feature388.Edge17]
  Diameter = 2
  Invert = false
  LeftHanded = false
  Length = 1
  LengthCustom = 9.5
  MatchOuter = false
  OffsetAngle = 0
  Placement = pos=(44,-12.3124,-24) rot=(1,0,0;1.5708rad)
  Thread = false
  Type = 81
FEATURE [Part::FeaturePython] Screw002  label="ST2.9x9.5-Screw005"  # WARN: FeaturePython — macro-defined, semantics opaque (R4)
  BaseObject = -> V3_Connector_Only_1 [Part__Feature388.Edge18]
  Diameter = 2
  Invert = false
  LeftHanded = false
  Length = 1
  LengthCustom = 9.5
  MatchOuter = false
  OffsetAngle = 0
  Placement = pos=(44,-12.3124,24) rot=(1,0,0;1.5708rad)
  Thread = false
  Type = 81
FEATURE [Part::FeaturePython] Screw003  label="ST2.9x9.5-Screw006"  # WARN: FeaturePython — macro-defined, semantics opaque (R4)
  BaseObject = -> V3_Connector_Only_1 [Part__Feature388.Edge262]
  Diameter = 2
  Invert = false
  LeftHanded = false
  Length = 1
  LengthCustom = 9.5
  MatchOuter = false
  OffsetAngle = 0
  Placement = pos=(-44,-12.3124,24) rot=(1,0,0;1.5708rad)
  Thread = false
  Type = 81
FEATURE [App::Part] Assembly  label="Assy_V3Connector_Board"
  AssemblyType = Part::Link
  Group = -> [LCS_Origin,Constraints,Variables,Configurations,ConnectorBoardv3_Carrier,V3_Connector_Only_1,Screw,Screw001,Screw002,Screw003]
  Origin = -> Origin
  Type = Assembly
FEATURE [Spreadsheet::Sheet] Spreadsheet  label="BOM"
  cells = A1=3; B1=4; C1='M3x10 mm self-tapping screw; D1='5-10 mm; A2=2; B2=1; C2='ConnectorBoardv3; D2='-; A3=1; B3=1; C3='ConnectorBoardv3_Carrier; D3='-; E3='PETG or PLA; A4='Position; B4='Quantity; C4='Part; D4='Dimensions; E4='Material
FEATURE [TechDraw::DrawSVGTemplate] Template
  EditableTexts = approval_person=GitHub PR; creator=Stefan; date_of_issue=20.03.2026; document_type=Assembly Drawing; general_tolerances=na; identification_number=na; language_code=EN; part_material=na; revision_index=AAA; scale=1 : 1; sheet_number=1 / 1; title=Assy_V3Connector_Board
  Height = 297
  Orientation = 0
  Template = <userpath>/Documents/PiTrac/3D Printed Parts/Enclosure Version 3/Assets/PiTrac_A4_Portrait_ISO5457_minimal.svg
  Width = 210
FEATURE [TechDraw::DrawViewSpreadsheet] Sheet
  CellEnd = E4
  CellStart = A1
  Font = osifont
  LineWidth = 0.35
  LockPosition = false
  Rotation = 0
  ScaleType = 2
  Source = -> Spreadsheet
  Symbol = <blob: 4591 chars omitted>
  TextSize = 12
  X = 115.863
  Y = 88.338
FEATURE [TechDraw::DrawProjGroupItem] View  label="Front"
  CoarseView = false
  Direction = (0,-1,0)
  Focus = 100
  HardHidden = false
  IsoCount = 0
  IsoHidden = false
  IsoVisible = false
  LockPosition = true
  Perspective = false
  Rotation = 0
  RotationVector = (1,0,0)
  ScaleType = 2
  ScrubCount = 1
  SeamHidden = false
  SeamVisible = false
  SmoothHidden = false
  SmoothVisible = true
  Source = -> [Assembly]
  Type = 0
  X = 0
  XDirection = (1,0,0)
  Y = 0
FEATURE [TechDraw::DrawProjGroupItem] View001
  CoarseView = false
  Direction = (0.57735,-0.57735,-0.57735)
  Focus = 100
  HardHidden = false
  IsoCount = 0
  IsoHidden = false
  IsoVisible = false
  LockPosition = false
  Perspective = false
  Rotation = 0
  RotationVector = (1,0,0)
  Scale = 0.5
  ScaleType = 2
  ScrubCount = 1
  SeamHidden = false
  SeamVisible = false
  SmoothHidden = false
  SmoothVisible = true
  Source = -> [Assembly]
  Type = 0
  X = 158.895
  XDirection = (0.707107,0,0.707107)
  Y = 134.295
FEATURE [TechDraw::DrawViewBalloon] Balloon
  BubbleShape = 0
  EndType = 0
  EndTypeScale = 1
  KinkLength = 5
  LockPosition = false
  OriginX = -52.3797
  OriginY = -28.3457
  Rotation = 0
  ScaleType = 0
  ShapeScale = 1
  SourceView = -> View
  Text = 1
  TextWrapLen = -1
  X = -42.9122
  Y = -45
FEATURE [TechDraw::DrawViewBalloon] Balloon001
  BubbleShape = 0
  EndType = 0
  EndTypeScale = 1
  KinkLength = 5
  LockPosition = false
  OriginX = 21.9174
  OriginY = -1.30268
  Rotation = 0
  ScaleType = 0
  ShapeScale = 1
  SourceView = -> View
  Text = 2
  TextWrapLen = -1
  X = 31.9542
  Y = -45
FEATURE [TechDraw::DrawViewBalloon] Balloon002
  BubbleShape = 0
  EndType = 0
  EndTypeScale = 1
  KinkLength = 5
  LockPosition = false
  OriginX = -43.5551
  OriginY = 18.9084
  Rotation = 0
  ScaleType = 0
  ShapeScale = 1
  SourceView = -> View
  Text = 3
  TextWrapLen = -1
  X = -23.5551
  Y = 45
FEATURE [TechDraw::DrawViewBalloon] Balloon003
  BubbleShape = 0
  EndType = 0
  EndTypeScale = 1
  KinkLength = 5
  LockPosition = false
  OriginX = 44.2277
  OriginY = 19.5981
  Rotation = 0
  ScaleType = 0
  ShapeScale = 1
  SourceView = -> View
  Text = 3
  TextWrapLen = -1
  X = 64.2277
  Y = 45
FEATURE [TechDraw::DrawViewBalloon] Balloon005
  BubbleShape = 0
  EndType = 0
  EndTypeScale = 1
  KinkLength = 5
  LockPosition = false
  OriginX = -43.4289
  OriginY = -28.7897
  Rotation = 0
  ScaleType = 0
  ShapeScale = 1
  SourceView = -> View
  Text = 3
  TextWrapLen = -1
  X = -15.4584
  Y = -45
FEATURE [TechDraw::DrawViewBalloon] Balloon006
  BubbleShape = 0
  EndType = 0
  EndTypeScale = 1
  KinkLength = 5
  LockPosition = false
  OriginX = 44.6905
  OriginY = -29.4843
  Rotation = 0
  ScaleType = 0
  ShapeScale = 1
  SourceView = -> View
  Text = 3
  TextWrapLen = -1
  X = 64.6905
  Y = -9.48434
FEATURE [TechDraw::DrawProjGroupItem] ProjItem  label="Left"
  CoarseView = false
  Direction = (-1,-1e-16,0)
  Focus = 100
  HardHidden = false
  IsoCount = 0
  IsoHidden = false
  IsoVisible = false
  LockPosition = false
  Perspective = false
  Rotation = 0
  RotationVector = (1,0,0)
  ScaleType = 0
  ScrubCount = 1
  SeamHidden = false
  SeamVisible = false
  SmoothHidden = false
  SmoothVisible = true
  Source = -> [Assembly]
  Type = 1
  X = 26.9737
  XDirection = (1e-16,-1,0)
  Y = 0
FEATURE [TechDraw::DrawProjGroup] ProjGroup
  Anchor = -> View
  AutoDistribute = true
  LockPosition = false
  ProjectionType = 0
  Rotation = 0
  ScaleType = 0
  Source = -> [Assembly]
  Views = -> [View,ProjItem]
  X = 83.6926
  Y = 220.778
  spacingX = 15
  spacingY = 15
FEATURE [TechDraw::DrawViewDimension] Dimension
  AngleOverride = false
  Arbitrary = false
  ArbitraryTolerances = false
  BoxCorners = (2) [(-55,-35.0053,-1e-07),(55,35.0053,1e-07)]
  EqualTolerance = true
  ExtensionAngle = 0
  FormatSpec = %.2w
  FormatSpecOverTolerance = %+.2w
  FormatSpecUnderTolerance = %+.2w
  Inverted = false
  LineAngle = 0
  LockPosition = false
  MeasureType = 1
  OverTolerance = 0
  References2D = -> [View]
  Rotation = 0
  ScaleType = 0
  TheoreticalExact = false
  Type = 0
  UnderTolerance = 0
  X = 0
  Y = -54.1451
FEATURE [TechDraw::DrawViewDimension] Dimension001
  AngleOverride = false
  Arbitrary = false
  ArbitraryTolerances = false
  BoxCorners = (2) [(-11.9737,-35.0053,-1e-07),(11.9737,35.0053,1e-07)]
  EqualTolerance = true
  ExtensionAngle = 0
  FormatSpec = %.2w
  FormatSpecOverTolerance = %+.2w
  FormatSpecUnderTolerance = %+.2w
  Inverted = false
  LineAngle = 0
  LockPosition = false
  MeasureType = 1
  OverTolerance = 0
  References2D = -> [ProjItem]
  Rotation = 0
  ScaleType = 0
  TheoreticalExact = false
  Type = 0
  UnderTolerance = 0
  X = 18.3809
  Y = 0.005286
FEATURE [TechDraw::DrawViewDimension] Dimension002
  AngleOverride = false
  Arbitrary = false
  ArbitraryTolerances = false
  BoxCorners = (2) [(-11.9737,-35.0053,-1e-07),(11.9737,35.0053,1e-07)]
  EqualTolerance = true
  ExtensionAngle = 0
  FormatSpec = %.2w
  FormatSpecOverTolerance = %+.2w
  FormatSpecUnderTolerance = %+.2w
  Inverted = false
  LineAngle = 0
  LockPosition = false
  MeasureType = 1
  OverTolerance = 0
  References2D = -> [ProjItem]
  Rotation = 0
  ScaleType = 0
  TheoreticalExact = false
  Type = 0
  UnderTolerance = 0
  X = -0.8
  Y = 50.6191
FEATURE [TechDraw::DrawPage] Page
  KeepUpdated = true
  NextBalloonIndex = 8
  ProjectionType = 0
  Template = -> Template
  Views = -> [Sheet,View001,Balloon,Balloon001,Balloon002,Balloon003,Balloon005,Balloon006,ProjGroup,Dimension,Dimension001,Dimension002]
FEATURE [TechDraw::DrawSVGTemplate] Template001
  Height = 210
  Orientation = 1
  Template = C:/Program Files/FreeCAD 1.0/data/Mod/TechDraw/Templates/Default_Template_A4_Landscape.svg
  Width = 297
FEATURE [TechDraw::DrawProjGroupItem] View002
  CoarseView = false
  Direction = (0.57735,-0.57735,-0.57735)
  Focus = 100
  HardHidden = false
  IsoCount = 0
  IsoHidden = false
  IsoVisible = false
  LockPosition = false
  Perspective = false
  Rotation = 0
  RotationVector = (1,0,0)
  Scale = 2
  ScaleType = 2
  ScrubCount = 1
  SeamHidden = false
  SeamVisible = false
  SmoothHidden = false
  SmoothVisible = true
  Source = -> [Assembly]
  Type = 0
  X = 148.5
  XDirection = (0.707107,0,0.707107)
  Y = 105
FEATURE [TechDraw::DrawPage] Page001
  KeepUpdated = true
  NextBalloonIndex = 1
  ProjectionType = 0
  Template = -> Template001
  Views = -> [View002]
